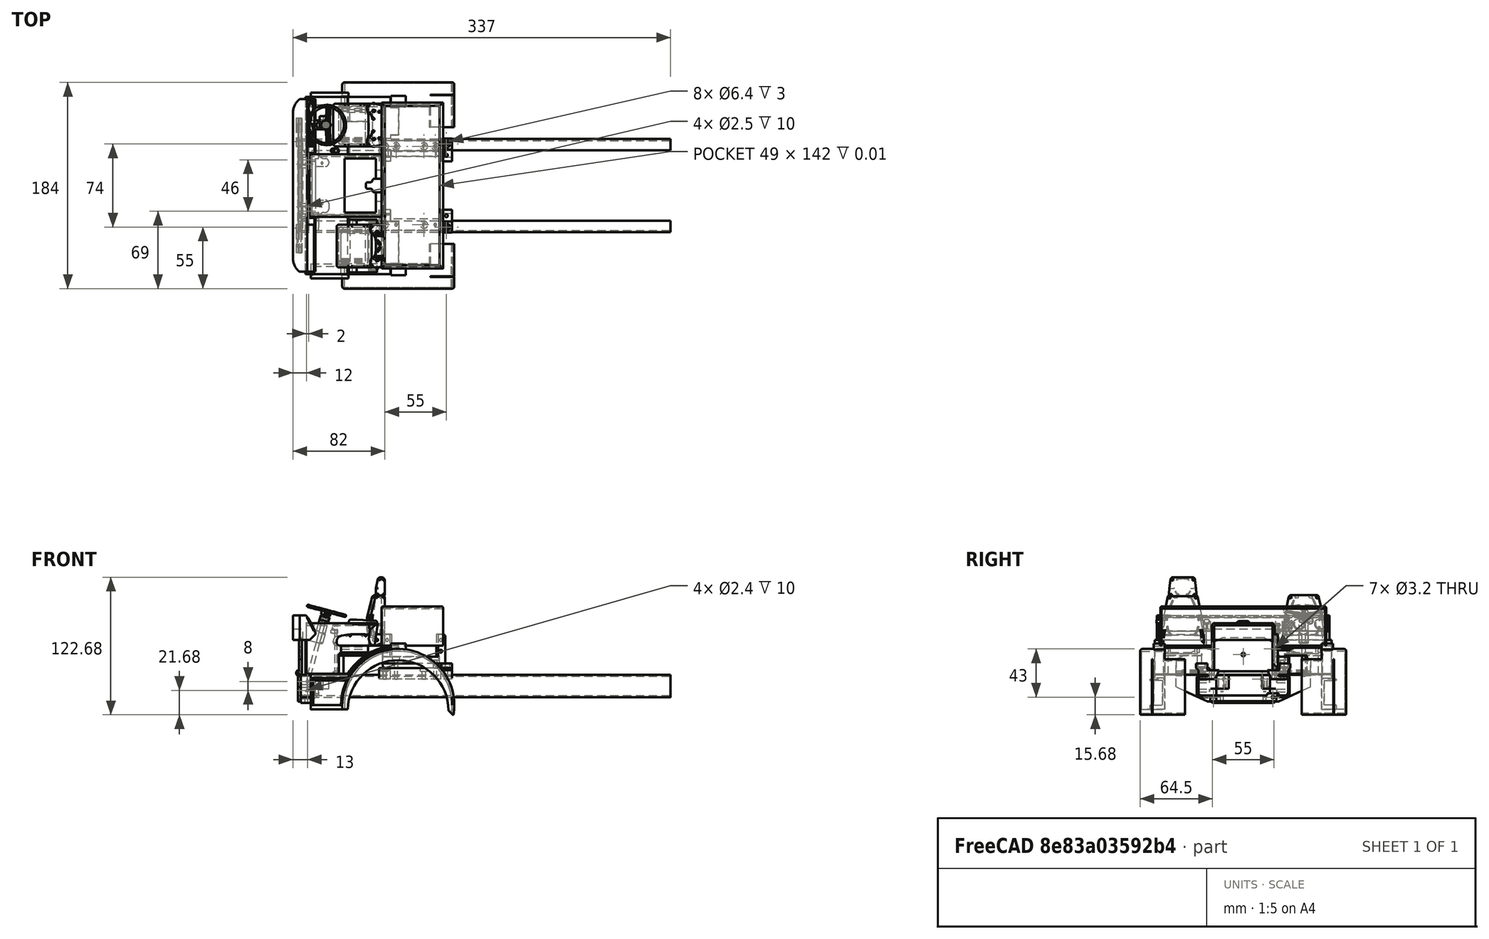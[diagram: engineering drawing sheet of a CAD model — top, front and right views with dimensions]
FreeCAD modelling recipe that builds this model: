
FCSTD DOCUMENT  (FreeCAD 0.16R6188 (Git))
Label: cab-internals
License: All rights reserved
LicenseURL: http://en.wikipedia.org/wiki/All_rights_reserved
objects: Part::Box×137, Part::Cylinder×127, Part::MultiFuse×110, Part::Cut×106, Part::Fillet×98, Part::Chamfer×51, Part::Mirroring×12, Part::Torus×1
note: 642 computed .brp shape members not serialized (recipe doc carries the construction recipe); baked Part::Feature solids carry a one-line shape summary decoded from their .brp

FEATURE [Part::Box] Box001  label="Cube001"
  Height = 64
  Length = 150
  Placement = pos=(0,-1,60) rot=(0,0,1;0rad)
  Width = 170
FEATURE [Part::MultiFuse] Fusion001
FEATURE [Part::Cut] Cut002
FEATURE [Part::Cylinder] Cylinder
  Angle = 360
  Height = 15
  Radius = 2.7
FEATURE [Part::Cylinder] Cylinder001
  Angle = 360
  Height = 15
  Radius = 2.7
FEATURE [Part::Fillet] Fillet008
  Base = -> Cylinder
  Edges = 2 edges r=2: [Edge1,Edge3]
  Placement = pos=(152.5,151,39) rot=(1,0,0;1.5708rad)
FEATURE [Part::Cylinder] Cylinder002
  Angle = 360
  Height = 15
  Radius = 2.7
FEATURE [Part::Fillet] Fillet011
  Base = -> Cylinder001
  Edges = 2 edges r=2: [Edge1,Edge3]
  Placement = pos=(152.5,151,31) rot=(1,0,0;1.5708rad)
FEATURE [Part::Fillet] Fillet012
  Base = -> Cylinder002
  Edges = 2 edges r=2: [Edge1,Edge3]
  Placement = pos=(152.5,31,31) rot=(1,0,0;1.5708rad)
FEATURE [Part::Cylinder] Cylinder004
  Angle = 360
  Height = 15
  Radius = 2.7
FEATURE [Part::Fillet] Fillet010
  Base = -> Cylinder004
  Edges = 2 edges r=2: [Edge1,Edge3]
  Placement = pos=(152.5,31,39) rot=(1,0,0;1.5708rad)
FEATURE [Part::MultiFuse] Fusion006
  Shapes = -> [Fillet008,Fillet010,Fillet011,Fillet012]
FEATURE [Part::MultiFuse] Fusion007
  Shapes = -> [Box001,Fusion006,Fusion001]
FEATURE [Part::Cut] Cut017  label="cab-lower"
  Base = -> Cut002
  Tool = -> Fusion007
FEATURE [Part::Cylinder] Cylinder005
  Angle = 198
  Height = 22
  Placement = pos=(98,168,-23) rot=(1,0,0;1.5708rad)
  Radius = 50
FEATURE [Part::Cylinder] Cylinder006
  Angle = 198
  Height = 22
  Placement = pos=(98.7,168,-28) rot=(1,0,0;1.5708rad)
  Radius = 45
FEATURE [Part::Cylinder] Cylinder003
  Angle = 198
  Height = 22
  Placement = pos=(98,167,-23) rot=(1,0,0;1.5708rad)
  Radius = 48
FEATURE [Part::Cut] Cut009
  Base = -> Cylinder005
  Tool = -> Cylinder006
FEATURE [Part::Cut] Cut010
  Base = -> Cut009
  Placement = pos=(5.48275,6,16.6681) rot=(0,1,0;0.174533rad)
  Tool = -> Cylinder003
FEATURE [Part::Cylinder] Cylinder007
  Angle = 360
  Height = 22
  Placement = pos=(98,174,-23) rot=(1,0,0;1.5708rad)
  Radius = 50
FEATURE [Part::Box] Box011  label="Cube011"
  Height = 27
  Length = 34
  Placement = pos=(20,152,-27) rot=(0,0,1;0rad)
  Width = 16
FEATURE [Part::Box] Box012  label="Cube012"
  Height = 27
  Length = 30
  Placement = pos=(32,152,-54) rot=(0,0,1;0rad)
  Width = 22
FEATURE [Part::Cut] Cut012
  Base = -> Box011
  Tool = -> Cylinder007
FEATURE [Part::Box] Box013  label="Cube013"
  Height = 22
  Length = 31
  Placement = pos=(22,162,-23) rot=(0,0,1;0rad)
  Width = 6
FEATURE [Part::Cylinder] Cylinder008
  Angle = 360
  Height = 22
  Placement = pos=(98,174,-23) rot=(1,0,0;1.5708rad)
  Radius = 50
FEATURE [Part::Cut] Cut016
  Base = -> Cut010
  Tool = -> Box012
FEATURE [Part::Box] Box015  label="Cube015"
  Height = 22
  Length = 35
  Placement = pos=(20,162,-23) rot=(0,0,1;0rad)
  Width = 6
FEATURE [Part::Box] Box016  label="Cube016"
  Height = 22
  Length = 31
  Placement = pos=(22,154,-23) rot=(0,0,1;0rad)
  Width = 8
FEATURE [Part::Cylinder] Cylinder009
  Angle = 360
  Height = 22
  Placement = pos=(98,174,-23) rot=(1,0,0;1.5708rad)
  Radius = 51
FEATURE [Part::Cut] Cut018
  Base = -> Box013
  Tool = -> Cylinder008
FEATURE [Part::Cut] Cut019
  Base = -> Box016
  Tool = -> Cylinder009
FEATURE [Part::Cut] Cut020
  Base = -> Cut012
  Tool = -> Cut018
FEATURE [Part::Cut] Cut021
  Base = -> Cut020
  Tool = -> Cut019
FEATURE [Part::Cut] Cut022
  Base = -> Cut021
  Tool = -> Box015
FEATURE [Part::MultiFuse] Fusion003
  Shapes = -> [Cut022,Cut016]
FEATURE [Part::Cut] Cut023
  Base = -> Cut021
  Tool = -> Box015
FEATURE [Part::Cut] Cut024
  Base = -> Cut010
  Tool = -> Box012
FEATURE [Part::MultiFuse] Fusion004  label="right-wing_00"
  Placement = pos=(0,1,0) rot=(0,0,1;0rad)
  Shapes = -> [Cut023,Cut024]
FEATURE [Part::Mirroring] Part__Mirroring  label="left-wing_00"
  Base = (0,0,0)
  Normal = (0,1,0)
  Placement = pos=(0,167,0) rot=(0,0,1;0rad)
  Source = -> Fusion003
FEATURE [Part::Cylinder] Cylinder018
  Angle = 360
  Height = 22
  Placement = pos=(98,189,-23) rot=(1,0,0;1.5708rad)
  Radius = 50
FEATURE [Part::Cylinder] Cylinder019
  Angle = 360
  Height = 22
  Placement = pos=(98,189,-23) rot=(1,0,0;1.5708rad)
  Radius = 82
FEATURE [Part::Cut] Cut088
  Base = -> Cylinder019
  Placement = pos=(0,-1,0) rot=(0,0,1;0rad)
  Tool = -> Cylinder018
FEATURE [Part::Cut] Cut089
  Base = -> Fusion004
  Tool = -> Cut088
FEATURE [Part::Cylinder] Cylinder020
  Angle = 360
  Height = 22
  Placement = pos=(98,189,-23) rot=(1,0,0;1.5708rad)
  Radius = 82
FEATURE [Part::Cylinder] Cylinder021
  Angle = 360
  Height = 22
  Placement = pos=(98,189,-23) rot=(1,0,0;1.5708rad)
  Radius = 50
FEATURE [Part::Cut] Cut090
  Base = -> Cylinder020
  Placement = pos=(0,-187,0) rot=(0,0,1;0rad)
  Tool = -> Cylinder021
FEATURE [Part::Cut] Cut091
  Base = -> Part__Mirroring
  Tool = -> Cut090
FEATURE [Part::Fillet] Fillet098
  Base = -> Cut091
  Edges = 1 edges r=2: [Edge58]
FEATURE [Part::Fillet] Fillet099
  Base = -> Cut089
  Edges = 1 edges r=2: [Edge58]
FEATURE [Part::Fillet] Fillet101
  Base = -> Fillet098
  Edges = 1 edges r=2: [Edge37]
FEATURE [Part::Box] Box188  label="Cube188"
  Height = 5.8
  Length = 13.6
  Placement = pos=(91.2,5,26) rot=(0,0,1;0rad)
  Width = 10
FEATURE [Part::Box] Box192  label="Cube192"
  Height = 5.8
  Length = 13.6
  Placement = pos=(91.2,153,26) rot=(0,0,1;0rad)
  Width = 10
FEATURE [Part::MultiFuse] Fusion078  label="left-wing_01"
  Shapes = -> [Fillet101,Box188]
FEATURE [Part::MultiFuse] Fusion079
  Shapes = -> [Box192,Fillet099]
FEATURE [Part::Fillet] Fillet102  label="right-wing_01"
  Base = -> Fusion079
  Edges = 1 edges r=2: [Edge72]
FEATURE [Part::Box] Box204  label="Cube204"
  Height = 10
  Length = 10
  Placement = pos=(140.3,-7,-39.5) rot=(0,-1,0;0.785398rad)
  Width = 40
FEATURE [Part::Cylinder] Cylinder043
  Angle = 65
  Height = 18
  Placement = pos=(98,153,-23) rot=(0.992433,0.086827,-0.086827;1.57839rad)
  Radius = 50
FEATURE [Part::Cylinder] Cylinder044
  Angle = 360
  Height = 18
  Placement = pos=(98,153,-23) rot=(1,0,0;1.5708rad)
  Radius = 48
FEATURE [Part::Cut] Cut107
  Base = -> Cylinder043
  Tool = -> Cylinder044
FEATURE [Part::Cylinder] Cylinder045
  Angle = 360
  Height = 18
  Placement = pos=(98,153,-23) rot=(1,0,0;1.5708rad)
  Radius = 48
FEATURE [Part::Cylinder] Cylinder046
  Angle = 65
  Height = 18
  Placement = pos=(98,153,-23) rot=(0.992433,0.086827,-0.086827;1.57839rad)
  Radius = 50
FEATURE [Part::Cut] Cut108
  Base = -> Cylinder046
  Placement = pos=(0,-120,0) rot=(0,0,1;0rad)
  Tool = -> Cylinder045
FEATURE [Part::MultiFuse] Fusion100
  Shapes = -> [Fusion078,Cut108]
FEATURE [Part::Cut] Cut109
  Base = -> Fusion100
  Placement = pos=(0,-2,0) rot=(0,0,1;0rad)
  Tool = -> Box204
FEATURE [Part::MultiFuse] Fusion101
  Shapes = -> [Cut107,Fillet102]
FEATURE [Part::Box] Box205  label="Cube205"
  Height = 10
  Length = 10
  Placement = pos=(140.3,135,-39.5) rot=(0,-1,0;0.785398rad)
  Width = 40
FEATURE [Part::Cut] Cut110
  Base = -> Fusion101
  Placement = pos=(0,2,0) rot=(0,0,1;0rad)
  Tool = -> Box205
FEATURE [Part::Cylinder] Cylinder047
  Angle = 65
  Height = 0.5
  Placement = pos=(98,153,-23) rot=(0.992433,0.086827,-0.086827;1.57839rad)
  Radius = 50
FEATURE [Part::Cylinder] Cylinder048
  Angle = 360
  Height = 0.5
  Placement = pos=(98,153,-23) rot=(1,0,0;1.5708rad)
  Radius = 49.5
FEATURE [Part::Cut] Cut111
  Base = -> Cylinder047
  Placement = pos=(0,-151,0) rot=(0,0,1;0rad)
  Tool = -> Cylinder048
FEATURE [Part::Cylinder] Cylinder049
  Angle = 65
  Height = 0.5
  Placement = pos=(98,153,-23) rot=(0.992433,0.086827,-0.086827;1.57839rad)
  Radius = 50
FEATURE [Part::Cylinder] Cylinder050
  Angle = 360
  Height = 0.5
  Placement = pos=(98,153,-23) rot=(1,0,0;1.5708rad)
  Radius = 49.5
FEATURE [Part::Cut] Cut112
  Base = -> Cylinder049
  Placement = pos=(0,13,0) rot=(0,0,1;0rad)
  Tool = -> Cylinder050
FEATURE [Part::Cut] Cut113  label="left-wing"
  Base = -> Cut109
  Placement = pos=(0,1,0) rot=(0,0,1;0rad)
  Tool = -> Cut111
FEATURE [Part::Cut] Cut114  label="right-wing"
  Base = -> Cut110
  Placement = pos=(0,-1,0) rot=(0,0,1;0rad)
  Tool = -> Cut112
FEATURE [Part::Box] Box007  label="Cube"
  Height = 20
  Length = 330
  Width = 10
FEATURE [Part::Box] Box008  label="Cube206"
  Height = 17
  Length = 430
  Placement = pos=(0,1.5,1.5) rot=(0,0,1;0rad)
  Width = 10
FEATURE [Part::Fillet] Fillet
  Base = -> Box007
  Edges = 2 edges r=3: [Edge9,Edge10]
FEATURE [Part::Fillet] Fillet001
  Base = -> Box008
  Edges = 2 edges r=2: [Edge9,Edge10]
FEATURE [Part::Cut] Cut003
  Base = -> Fillet
  Tool = -> Fillet001
FEATURE [Part::Fillet] Fillet002
  Base = -> Box007
  Edges = 2 edges r=3: [Edge9,Edge10]
FEATURE [Part::Fillet] Fillet003
  Base = -> Box008
  Edges = 2 edges r=2: [Edge9,Edge10]
FEATURE [Part::Cut] Cut004
  Base = -> Fillet002
  Placement = pos=(0,-1.5,0) rot=(0,0,1;0rad)
  Tool = -> Fillet003
FEATURE [Part::Mirroring] Part__Mirroring001  label="Cut (Mirror #1)"
  Base = (0,0,0)
  Normal = (0,1,0)
  Placement = pos=(0,81.5,0) rot=(0,0,1;0rad)
  Source = -> Cut003
FEATURE [Part::Fillet] Fillet004  label="lower-plate_00"
  Edges = 2 edges r=0.25: [Edge74,Edge75]
  Placement = pos=(-3,100,59) rot=(-0.57735,0.57735,0.57735;4.18879rad)
FEATURE [Part::Cylinder] Cylinder051
  Angle = 360
  Height = 11
  Placement = pos=(-2,66.5,-1) rot=(0,1,0;1.5708rad)
  Radius = 1.25
FEATURE [Part::Cylinder] Cylinder010
  Angle = 360
  Height = 11
  Placement = pos=(-2,13.5,-1) rot=(0,1,0;1.5708rad)
  Radius = 1.25
FEATURE [Part::Cylinder] Cylinder011
  Angle = 360
  Height = 15
  Placement = pos=(-2,23,15) rot=(0,1,0;1.5708rad)
  Radius = 1.25
FEATURE [Part::Cylinder] Cylinder012
  Angle = 360
  Height = 15
  Placement = pos=(-2,57,15) rot=(0,1,0;1.5708rad)
  Radius = 1.25
FEATURE [Part::MultiFuse] Fusion010
  Placement = pos=(0,0,1) rot=(0,0,1;0rad)
  Shapes = -> [Cylinder051,Cylinder011,Cylinder010,Cylinder012]
FEATURE [Part::Cut] Cut005
  Tool = -> Fusion010
FEATURE [Part::Cylinder] Cylinder013
  Angle = 360
  Height = 2.5
  Placement = pos=(-4.5,12.5,-1) rot=(0,1,0;1.5708rad)
  Radius = 2
FEATURE [Part::Cylinder] Cylinder014
  Angle = 360
  Height = 2.5
  Placement = pos=(-4.5,67.5,-1) rot=(0,1,0;1.5708rad)
  Radius = 2
FEATURE [Part::Cylinder] Cylinder015
  Angle = 360
  Height = 11
  Placement = pos=(-7,66.5,-1) rot=(0,1,0;1.5708rad)
  Radius = 1.6
FEATURE [Part::Cylinder] Cylinder016
  Angle = 360
  Height = 11
  Placement = pos=(-7,13.5,-1) rot=(0,1,0;1.5708rad)
  Radius = 1.6
FEATURE [Part::MultiFuse] Fusion011
  Shapes = -> [Cylinder016,Cylinder015]
FEATURE [Part::MultiFuse] Fusion012
  Shapes = -> [Cylinder014,Cylinder013]
FEATURE [Part::MultiFuse] Fusion013
  Shapes = -> [Fillet004,Fusion012]
FEATURE [Part::Cut] Cut006  label="cab_tilt_lower001"
  Base = -> Fusion013
  Placement = pos=(13,44,-15) rot=(0,0,1;0rad)
  Tool = -> Fusion011
FEATURE [Part::Fillet] Fillet009
  Base = -> Cut005
  Edges = 2 edges r=3: [Edge4,Edge16]
FEATURE [Part::MultiFuse] Fusion015  label="frame-bars001"
  Placement = pos=(11,44,-16) rot=(0,0,1;0rad)
  Shapes = -> [Cut004,Part__Mirroring001]
FEATURE [Part::Cut] Cut007  label="cab_tilt_upper001"
  Placement = pos=(11,144,37) rot=(0.57735,-0.57735,-0.57735;2.0944rad)
FEATURE [Part::Cylinder] Cylinder033
  Angle = 360
  Height = 10
  Placement = pos=(-8,25.5,0) rot=(0,0,1;0rad)
  Radius = 1.2
FEATURE [Part::Cylinder] Cylinder034
  Angle = 360
  Height = 10
  Placement = pos=(-8,33.5,0) rot=(0,0,1;0rad)
  Radius = 1.2
FEATURE [Part::MultiFuse] Fusion022
  Placement = pos=(12,80,-19.5) rot=(1,0,0;1.5708rad)
  Shapes = -> [Cylinder034,Cylinder033]
FEATURE [Part::Cylinder] Cylinder035
  Angle = 360
  Height = 10
  Placement = pos=(-8,33.5,0) rot=(0,0,1;0rad)
  Radius = 1.2
FEATURE [Part::Cylinder] Cylinder036
  Angle = 360
  Height = 10
  Placement = pos=(-8,25.5,0) rot=(0,0,1;0rad)
  Radius = 1.2
FEATURE [Part::MultiFuse] Fusion023
  Placement = pos=(12,10,-19.5) rot=(1,0,0;1.5708rad)
  Shapes = -> [Cylinder035,Cylinder036]
FEATURE [Part::MultiFuse] Fusion024
  Shapes = -> [Fusion022,Fusion023]
FEATURE [Part::Cut] Cut115  label="front-cross-member__"
  Base = -> Fillet009
  Tool = -> Fusion024
FEATURE [Part::Box] Box031
  Height = 1
  Length = 16
  Placement = pos=(-2,9,18.5) rot=(0,0,1;0rad)
  Width = 62
FEATURE [Part::MultiFuse] Fusion041  label="front-cross-member_"
  Shapes = -> [Cut115,Box031]
FEATURE [Part::Box] Box035  label="Cube024"
  Height = 25
  Length = 7
  Placement = pos=(8,16,-5) rot=(0,0,1;0rad)
  Width = 48
FEATURE [Part::Cut] Cut046
  Base = -> Fusion041
  Tool = -> Box035
FEATURE [Part::Box] Box036  label="Cube025"
  Height = 12
  Length = 15
  Placement = pos=(8,16,7.5) rot=(0,0,1;0rad)
  Width = 7
FEATURE [Part::Box] Box038  label="Cube027"
  Height = 18
  Length = 3
  Placement = pos=(8,16,1.5) rot=(0,0,1;0rad)
  Width = 48
FEATURE [Part::Box] Box039  label="Cube028"
  Height = 12
  Length = 12
  Placement = pos=(11,53,7.5) rot=(0,0,1;0rad)
  Width = 11
FEATURE [Part::Cylinder] Cylinder059
  Angle = 360
  Height = 15
  Placement = pos=(17,19.5,1.5) rot=(0,0,1;0rad)
  Radius = 0.9
FEATURE [Part::Cylinder] Cylinder060
  Angle = 360
  Height = 15
  Placement = pos=(17,55.5,1.5) rot=(0,0,1;0rad)
  Radius = 0.9
FEATURE [Part::MultiFuse] Fusion044
  Placement = pos=(0,0.5,4) rot=(0,0,1;0rad)
  Shapes = -> [Cylinder059,Cylinder060]
FEATURE [Part::Cylinder] Cylinder061
  Angle = 360
  Height = 10
  Placement = pos=(-2,23,16) rot=(0,1,0;1.5708rad)
  Radius = 1.25
FEATURE [Part::Cylinder] Cylinder062
  Angle = 360
  Height = 10
  Placement = pos=(-2,57,16) rot=(0,1,0;1.5708rad)
  Radius = 1.25
FEATURE [Part::MultiFuse] Fusion045
  Shapes = -> [Cylinder062,Cylinder061]
FEATURE [Part::Cylinder] Cylinder063
  Angle = 360
  Height = 10
  Placement = pos=(-2,23,16) rot=(0,1,0;1.5708rad)
  Radius = 1.25
FEATURE [Part::Cylinder] Cylinder064
  Angle = 360
  Height = 10
  Placement = pos=(-2,57,16) rot=(0,1,0;1.5708rad)
  Radius = 1.25
FEATURE [Part::MultiFuse] Fusion046
  Placement = pos=(0,0,-6) rot=(0,0,1;0rad)
  Shapes = -> [Cylinder064,Cylinder063]
FEATURE [Part::MultiFuse] Fusion047
  Shapes = -> [Cut046,Box036,Box038,Box039]
FEATURE [Part::Cut] Cut047
  Base = -> Fusion047
  Tool = -> Fusion044
FEATURE [Part::MultiFuse] Fusion048
  Shapes = -> [Fusion045,Cut047]
FEATURE [Part::Cut] Cut048
  Base = -> Fusion048
  Tool = -> Fusion046
FEATURE [Part::Mirroring] Part__Mirroring006  label="Cut048 (Mirror #5)"
  Base = (0,0,0)
  Normal = (0,1,0)
  Source = -> Cut048
FEATURE [Part::Fillet] Fillet034
  Base = -> Part__Mirroring006
  Edges = 2 edges r=5: [Edge102,Edge118]
FEATURE [Part::Fillet] Fillet035
  Base = -> Fillet034
  Edges = 4 edges r=3: [Edge33,Edge54,Edge77,Edge79]
FEATURE [Part::Box] Box040
  Height = 10
  Length = 10
  Placement = pos=(8,-18.5,-6.5) rot=(0,0,1;0rad)
  Width = 10
FEATURE [Part::Cut] Cut049
  Base = -> Fillet035
  Tool = -> Box040
FEATURE [Part::Cylinder] Cylinder065
  Angle = 360
  Height = 10
  Placement = pos=(3,-59,-5) rot=(0,0,1;0rad)
  Radius = 1.25
FEATURE [Part::Cylinder] Cylinder066
  Angle = 360
  Height = 10
  Placement = pos=(3,-21,-5) rot=(0,0,1;0rad)
  Radius = 1.25
FEATURE [Part::MultiFuse] Fusion049
  Shapes = -> [Cylinder065,Cylinder066]
FEATURE [Part::Cylinder] Cylinder067
  Angle = 360
  Height = 10
  Placement = pos=(5,-63,9.5) rot=(0,0,1;0rad)
  Radius = 1.25
FEATURE [Part::Cylinder] Cylinder068
  Angle = 360
  Height = 10
  Placement = pos=(5,-17,9.5) rot=(0,0,1;0rad)
  Radius = 1.25
FEATURE [Part::MultiFuse] Fusion050
  Shapes = -> [Cylinder067,Cylinder068]
FEATURE [Part::Cut] Cut050
  Base = -> Cut049
  Tool = -> Fusion049
FEATURE [Part::Cut] Cut051  label="front-cross-member"
  Base = -> Cut050
  Placement = pos=(13,124,-16) rot=(0,0,1;0rad)
  Tool = -> Fusion050
FEATURE [Part::Box] Box  label="Cube207"
  Height = 10
  Length = 65
  Width = 80
FEATURE [Part::Box] Box206  label="Cube208"
  Height = 10
  Length = 65
  Placement = pos=(0,19,0) rot=(0,0,1;0rad)
  Width = 42
FEATURE [Part::Cylinder] Cylinder069
  Angle = 360
  Height = 10
  Radius = 1.25
FEATURE [Part::Cylinder] Cylinder070
  Angle = 360
  Height = 10
  Placement = pos=(0,54,0) rot=(0,0,1;0rad)
  Radius = 1.25
FEATURE [Part::MultiFuse] Fusion
  Placement = pos=(5,13,0) rot=(0,0,1;0rad)
  Shapes = -> [Cylinder069,Cylinder070]
FEATURE [Part::Cylinder] Cylinder071
  Angle = 360
  Height = 10
  Placement = pos=(0,54,0) rot=(0,0,1;0rad)
  Radius = 1.25
FEATURE [Part::Cylinder] Cylinder072
  Angle = 360
  Height = 10
  Radius = 1.25
FEATURE [Part::MultiFuse] Fusion102
  Placement = pos=(60,13,0) rot=(0,0,1;0rad)
  Shapes = -> [Cylinder072,Cylinder071]
FEATURE [Part::MultiFuse] Fusion002
  Shapes = -> [Fusion,Fusion102]
FEATURE [Part::Cylinder] Cylinder073
  Angle = 360
  Height = 10
  Placement = pos=(5,0,0) rot=(0,0,1;0rad)
  Radius = 1.6
FEATURE [Part::Cylinder] Cylinder074
  Angle = 360
  Height = 10
  Placement = pos=(5,70,0) rot=(0,0,1;0rad)
  Radius = 1.6
FEATURE [Part::MultiFuse] Fusion103
  Placement = pos=(0,5,0) rot=(0,0,1;0rad)
  Shapes = -> [Cylinder074,Cylinder073]
FEATURE [Part::Cylinder] Cylinder075
  Angle = 360
  Height = 3
  Placement = pos=(5,70,0) rot=(0,0,1;0rad)
  Radius = 3.2
FEATURE [Part::Cylinder] Cylinder076
  Angle = 360
  Height = 3
  Placement = pos=(5,0,0) rot=(0,0,1;0rad)
  Radius = 3.2
FEATURE [Part::MultiFuse] Fusion104
  Placement = pos=(0,5,7) rot=(0,0,1;0rad)
  Shapes = -> [Cylinder075,Cylinder076]
FEATURE [Part::MultiFuse] Fusion005
  Placement = pos=(55,0,0) rot=(0,0,1;0rad)
  Shapes = -> [Fusion103,Fusion104]
FEATURE [Part::MultiFuse] Fusion105
  Placement = pos=(0,5,7) rot=(0,0,1;0rad)
  Shapes = -> [Cylinder075,Cylinder076]
FEATURE [Part::MultiFuse] Fusion008
  Placement = pos=(0,5,0) rot=(0,0,1;0rad)
  Shapes = -> [Cylinder074,Cylinder073]
FEATURE [Part::MultiFuse] Fusion106
  Placement = pos=(20,0,0) rot=(0,0,1;0rad)
  Shapes = -> [Fusion008,Fusion105]
FEATURE [Part::MultiFuse] Fusion009
  Shapes = -> [Fusion005,Fusion106]
FEATURE [Part::Cylinder] Cylinder077
  Angle = 360
  Height = 10
  Placement = pos=(0,70,0) rot=(0,0,1;0rad)
  Radius = 1.25
FEATURE [Part::Cylinder] Cylinder078
  Angle = 360
  Height = 10
  Radius = 1.25
FEATURE [Part::Box] Box002  label="Cube002"
  Height = 10
  Length = 10
  Placement = pos=(0,-2,4) rot=(0,0,1;0rad)
  Width = 10
FEATURE [Part::Chamfer] Chamfer002
  Base = -> Box002
  Edges = 1 edges r=6: [Edge9]
FEATURE [Part::Cut] Cut
  Base = -> Box
  Tool = -> Box206
FEATURE [Part::Box] Box003
  Height = 10
  Length = 45
  Placement = pos=(10,10,0) rot=(0,0,1;0rad)
  Width = 9
FEATURE [Part::Box] Box004
  Height = 10
  Length = 45
  Placement = pos=(10,61,0) rot=(0,0,1;0rad)
  Width = 9
FEATURE [Part::MultiFuse] Fusion107
  Shapes = -> [Box003,Box004]
FEATURE [Part::Cut] Cut116
  Base = -> Cut
  Tool = -> Fusion107
FEATURE [Part::Cut] Cut117
  Base = -> Cut116
  Tool = -> Fusion002
FEATURE [Part::MultiFuse] Fusion108
  Placement = pos=(50,5,0) rot=(0,0,1;0rad)
  Shapes = -> [Cylinder077,Cylinder078]
FEATURE [Part::Cylinder] Cylinder079
  Angle = 360
  Height = 10
  Radius = 1.25
FEATURE [Part::Cylinder] Cylinder080
  Angle = 360
  Height = 10
  Placement = pos=(0,70,0) rot=(0,0,1;0rad)
  Radius = 1.25
FEATURE [Part::MultiFuse] Fusion109
  Placement = pos=(15,5,0) rot=(0,0,1;0rad)
  Shapes = -> [Cylinder080,Cylinder079]
FEATURE [Part::Box] Box005
  Height = 12
  Length = 65
  Placement = pos=(0,15,0) rot=(-1,0,0;0.401426rad)
  Width = 10
FEATURE [Part::Mirroring] Part__Mirroring007  label="Box005 (Mirror #1)"
  Base = (0,0,0)
  Normal = (0,1,0)
  Placement = pos=(0,80,0) rot=(0,0,1;0rad)
  Source = -> Box005
FEATURE [Part::Box] Box006
  Height = 12
  Length = 65
  Placement = pos=(0,15,0) rot=(-1,0,0;0.401426rad)
  Width = 10
FEATURE [Part::MultiFuse] Fusion110
  Shapes = -> [Part__Mirroring007,Box006]
FEATURE [Part::Cut] Cut008
  Base = -> Cut117
  Tool = -> Fusion110
FEATURE [Part::MultiFuse] Fusion014
  Shapes = -> [Fusion009,Fusion108,Fusion109]
FEATURE [Part::Cut] Cut118
  Base = -> Cut008
  Tool = -> Fusion014
FEATURE [Part::Box] Box207  label="Cube003"
  Height = 10
  Length = 10
  Placement = pos=(0,-2,4) rot=(0,0,1;0rad)
  Width = 10
FEATURE [Part::Chamfer] Chamfer
  Base = -> Box207
  Edges = 1 edges r=6: [Edge9]
FEATURE [Part::Mirroring] Part__Mirroring008  label="Chamfer (Mirror #2)"
  Base = (0,0,0)
  Normal = (0,1,0)
  Placement = pos=(0,80,0) rot=(0,0,1;0rad)
  Source = -> Chamfer
FEATURE [Part::MultiFuse] Fusion111
  Shapes = -> [Chamfer002,Cut118,Part__Mirroring008]
FEATURE [Part::Cylinder] Cylinder081
  Angle = 360
  Height = 10
  Placement = pos=(5,3,4) rot=(0,0,1;0rad)
  Radius = 1.25
FEATURE [Part::Cylinder] Cylinder017
  Angle = 360
  Height = 3
  Placement = pos=(5,3,11) rot=(0,0,1;0rad)
  Radius = 3.2
FEATURE [Part::MultiFuse] Fusion016
  Shapes = -> [Cylinder081,Cylinder017]
FEATURE [Part::Cylinder] Cylinder082
  Angle = 360
  Height = 3
  Placement = pos=(5,3,11) rot=(0,0,1;0rad)
  Radius = 3.2
FEATURE [Part::Cylinder] Cylinder083
  Angle = 360
  Height = 10
  Placement = pos=(5,3,4) rot=(0,0,1;0rad)
  Radius = 1.25
FEATURE [Part::MultiFuse] Fusion017
  Placement = pos=(0,74,0) rot=(0,0,1;0rad)
  Shapes = -> [Cylinder083,Cylinder082]
FEATURE [Part::MultiFuse] Fusion018
  Shapes = -> [Fusion016,Fusion017]
FEATURE [Part::Cut] Cut119
  Base = -> Fusion111
  Tool = -> Fusion018
FEATURE [Part::Box] Box208
  Height = 2
  Length = 10
  Placement = pos=(0,8,8) rot=(0,0,1;0rad)
  Width = 11
FEATURE [Part::Box] Box009
  Height = 2
  Length = 10
  Placement = pos=(0,61,8) rot=(0,0,1;0rad)
  Width = 11
FEATURE [Part::Box] Box010
  Height = 2
  Length = 10
  Placement = pos=(55,8,8) rot=(0,0,1;0rad)
  Width = 11
FEATURE [Part::Box] Box209
  Height = 2
  Length = 10
  Placement = pos=(55,61,8) rot=(0,0,1;0rad)
  Width = 11
FEATURE [Part::MultiFuse] Fusion019
  Shapes = -> [Box208,Box010,Box209,Box009]
FEATURE [Part::Cut] Cut011  label="gearbox-holder"
  Base = -> Cut119
  Placement = pos=(146,124,0) rot=(0,0,1;3.14159rad)
  Tool = -> Fusion019
FEATURE [Part::Box] Box210
  Height = 5
  Length = 56
  Placement = pos=(-14,1,0) rot=(0,0,1;0rad)
  Width = 10
FEATURE [Part::Cut] Cut120
  Placement = pos=(-18,19,0) rot=(0,0,1;0rad)
FEATURE [Part::Fillet] Fillet103
  Base = -> Cut120
  Edges = 1 edges r=0.6: [Edge14]
  Placement = pos=(29,0,0) rot=(0,0,1;0rad)
FEATURE [Part::Box] Box211
  Height = 10
  Length = 17
  Placement = pos=(20,22,0) rot=(0,0,1;0rad)
  Width = 10
FEATURE [Part::Box] Box014
  Height = 10
  Length = 9
  Placement = pos=(20,11,0) rot=(0,0,1;0rad)
  Width = 21
FEATURE [Part::MultiFuse] Fusion020
  Shapes = -> [Box211,Box014]
FEATURE [Part::Cut] Cut013
  Base = -> Fillet103
  Tool = -> Fusion020
FEATURE [Part::Box] Box212
  Height = 3.4
  Length = 21
  Placement = pos=(8,11,0) rot=(0,0,1;0rad)
  Width = 5
FEATURE [Part::MultiFuse] Fusion021
  Shapes = -> [Box210,Cut013,Box212]
FEATURE [Part::Box] Box213
  Height = 5
  Length = 8
  Placement = pos=(34,-19,0) rot=(0,0,1;0rad)
  Width = 20
FEATURE [Part::Box] Box017
  Height = 5
  Length = 8
  Placement = pos=(-14,-19,0) rot=(0,0,1;0rad)
  Width = 20
FEATURE [Part::Cylinder] Cylinder084
  Angle = 360
  Height = 10
  Placement = pos=(-10,0,0) rot=(0,0,1;0rad)
  Radius = 1.25
FEATURE [Part::Cylinder] Cylinder085
  Angle = 360
  Height = 10
  Placement = pos=(-10,-10,0) rot=(0,0,1;0rad)
  Radius = 1.25
FEATURE [Part::MultiFuse] Fusion112
  Placement = pos=(0,-4,0) rot=(0,0,1;0rad)
  Shapes = -> [Cylinder085,Cylinder084]
FEATURE [Part::Cylinder] Cylinder022
  Angle = 360
  Height = 10
  Placement = pos=(-10,0,0) rot=(0,0,1;0rad)
  Radius = 1.25
FEATURE [Part::Cylinder] Cylinder023
  Angle = 360
  Height = 10
  Placement = pos=(-10,-10,0) rot=(0,0,1;0rad)
  Radius = 1.25
FEATURE [Part::MultiFuse] Fusion113
  Placement = pos=(48,-4,0) rot=(0,0,1;0rad)
  Shapes = -> [Cylinder023,Cylinder022]
FEATURE [Part::Box] Box018
  Height = 3.4
  Length = 17
  Placement = pos=(-9,11,0) rot=(0,0,1;0rad)
  Width = 15
FEATURE [Part::MultiFuse] Fusion114
  Shapes = -> [Fusion112,Fusion113]
FEATURE [Part::Cylinder] Cylinder024
  Angle = 360
  Height = 10
  Placement = pos=(5,19,0) rot=(0,0,1;0rad)
  Radius = 1.6
FEATURE [Part::Cylinder] Cylinder025
  Angle = 360
  Height = 10
  Placement = pos=(-6,19,0) rot=(0,0,1;0rad)
  Radius = 1.6
FEATURE [Part::MultiFuse] Fusion025
  Shapes = -> [Cylinder024,Cylinder025]
FEATURE [Part::Cut] Cut014
  Base = -> Box018
  Tool = -> Fusion025
FEATURE [Part::MultiFuse] Fusion026
  Shapes = -> [Box213,Box017,Cut014,Fusion021]
FEATURE [Part::Cut] Cut015
  Base = -> Fusion026
  Tool = -> Fusion114
FEATURE [Part::Fillet] Fillet104
  Base = -> Cut015
  Edges = 6 edges r=2: [Edge51,Edge54,Edge56,Edge58,Edge59,Edge61]
FEATURE [Part::Fillet] Fillet105
  Base = -> Fillet104
  Edges = 1 edges r=1.5: [Edge36]
FEATURE [Part::Fillet] Fillet106
  Base = -> Fillet105
  Edges = 2 edges r=3: [Edge30,Edge33]
FEATURE [Part::Box] Box019
  Height = 1.6
  Length = 19
  Placement = pos=(-10,10,3.4) rot=(0,0,1;0rad)
  Width = 10
FEATURE [Part::Cut] Cut121
  Base = -> Fillet106
  Tool = -> Box019
FEATURE [Part::Fillet] Fillet107
  Base = -> Cut121
  Edges = 2 edges r=2: [Edge42,Edge63]
FEATURE [Part::Box] Box020
  Height = 1
  Length = 4
  Placement = pos=(-2.5,25,0) rot=(0,0,1;0rad)
  Width = 1
FEATURE [Part::Cut] Cut122
  Base = -> Fillet107
  Tool = -> Box020
FEATURE [Part::Fillet] Fillet005
  Base = -> Cut122
  Edges = 1 edges r=0.99: [Edge94]
FEATURE [Part::Chamfer] Chamfer003
  Base = -> Fillet005
  Edges = 2 edges r=1.5: [Edge34,Edge36]
FEATURE [Part::MultiFuse] Fusion027
  Placement = pos=(48,-4,0) rot=(0,0,1;0rad)
  Shapes = -> [Cylinder023,Cylinder022]
FEATURE [Part::MultiFuse] Fusion029
  Placement = pos=(0,-4,0) rot=(0,0,1;0rad)
  Shapes = -> [Cylinder085,Cylinder084]
FEATURE [Part::MultiFuse] Fusion028
  Shapes = -> [Fusion029,Fusion027]
FEATURE [Part::Box] Box021
  Height = 5
  Length = 8
  Placement = pos=(34,-19,2) rot=(0,0,1;0rad)
  Width = 25
FEATURE [Part::Box] Box022
  Height = 5
  Length = 8
  Placement = pos=(-14,-19,2) rot=(0,0,1;0rad)
  Width = 25
FEATURE [Part::MultiFuse] Fusion030
  Shapes = -> [Box021,Box022]
FEATURE [Part::Cut] Cut123
  Base = -> Fusion030
  Tool = -> Fusion028
FEATURE [Part::Fillet] Fillet006
  Base = -> Cut123
  Edges = 2 edges r=2: [Edge6,Edge23]
FEATURE [Part::Chamfer] Chamfer004
  Base = -> Fillet006
  Edges = 2 edges r=2: [Edge18,Edge31]
FEATURE [Part::MultiFuse] Fusion031
  Placement = pos=(0,0,21) rot=(-1,0,0;1.5708rad)
  Shapes = -> [Chamfer003,Chamfer004]
FEATURE [Part::Box] Box023
  Height = 15
  Length = 53
  Placement = pos=(-13,0,-5) rot=(0,0,1;0rad)
  Width = 10
FEATURE [Part::Cut] Cut124
  Base = -> Fusion031
  Placement = pos=(0,0,0) rot=(0,0,1;3.14159rad)
  Tool = -> Box023
FEATURE [Part::Box] Box024
  Height = 1
  Length = 19
  Placement = pos=(-9,-5,10) rot=(0,0,1;0rad)
  Width = 5
FEATURE [Part::MultiFuse] Fusion032
  Placement = pos=(53,0,0) rot=(0,0,1;0rad)
  Shapes = -> [Cut124,Box024]
FEATURE [Part::Cylinder] Cylinder026
  Angle = 360
  Height = 10
  Placement = pos=(15,5,10) rot=(0,0,1;0rad)
  Radius = 1.6
FEATURE [Part::Cylinder] Cylinder027
  Angle = 360
  Height = 10
  Placement = pos=(50,5,10) rot=(0,0,1;0rad)
  Radius = 1.6
FEATURE [Part::Box] Box025
  Height = 10
  Length = 43
  Placement = pos=(11,0,10) rot=(0,0,1;0rad)
  Width = 10
FEATURE [Part::Fillet] Fillet007
  Base = -> Box025
  Edges = 1 edges r=3: [Edge4]
  Placement = pos=(0,-1,0) rot=(0,0,1;0rad)
FEATURE [Part::Cylinder] Cylinder028
  Angle = 360
  Height = 3
  Placement = pos=(15,5,17) rot=(0,0,1;0rad)
  Radius = 3.2
FEATURE [Part::Cylinder] Cylinder029
  Angle = 360
  Height = 3
  Placement = pos=(50,5,17) rot=(0,0,1;0rad)
  Radius = 3.2
FEATURE [Part::MultiFuse] Fusion034
  Shapes = -> [Cylinder026,Cylinder027,Cylinder028,Cylinder029]
FEATURE [Part::Box] Box026
  Height = 33
  Length = 56
  Placement = pos=(11,-15,10) rot=(0,0,1;0rad)
  Width = 10
FEATURE [Part::Box] Box027
  Height = 10
  Length = 13
  Placement = pos=(54,0,10) rot=(0,0,1;0rad)
  Width = 10
FEATURE [Part::Fillet] Fillet108
  Base = -> Box027
  Edges = 1 edges r=3: [Edge8]
  Placement = pos=(-5,-1,0) rot=(0,0,1;0rad)
FEATURE [Part::Cut] Cut125
  Base = -> Fusion032
  Placement = pos=(-5,14,0) rot=(0,0,1;0rad)
  Tool = -> Box026
FEATURE [Part::MultiFuse] Fusion035
  Placement = pos=(0,1,0) rot=(0,0,1;0rad)
  Shapes = -> [Fillet108,Fillet007]
FEATURE [Part::MultiFuse] Fusion036
  Shapes = -> [Cut125,Fusion035]
FEATURE [Part::Cut] Cut126
  Base = -> Fusion036
  Tool = -> Fusion034
FEATURE [Part::Box] Box028  label="Cube004"
  Height = 10
  Length = 56
  Placement = pos=(6,15,2) rot=(1,0,0;0.698132rad)
  Width = 10
FEATURE [Part::Cut] Cut127  label="steering-servo-holder"
  Base = -> Cut126
  Placement = pos=(146,124,0) rot=(0,0,1;3.14159rad)
  Tool = -> Box028
FEATURE [Part::Box] Box214  label="Cube209"
  Height = 22
  Length = 10
  Placement = pos=(4,7,35) rot=(0,0,1;0rad)
  Width = 154
FEATURE [Part::Box] Box215  label="Cube210"
  Height = 22
  Length = 10
  Placement = pos=(14,7,35) rot=(0,0,1;0rad)
  Width = 154
FEATURE [Part::Chamfer] Chamfer005
  Base = -> Box215
  Edges = 1 edges: [Edge6 r1=15 r2=8]
FEATURE [Part::Chamfer] Chamfer006
  Base = -> Chamfer005
  Edges = 1 edges r=5: [Edge3]
FEATURE [Part::MultiFuse] Fusion115
  Shapes = -> [Box214,Chamfer006]
FEATURE [Part::Box] Box216  label="Cube211"
  Height = 22
  Length = 17
  Placement = pos=(4,4,35) rot=(0,0,1;0rad)
  Width = 160
FEATURE [Part::Box] Box217  label="Cube212"
  Height = 22
  Length = 18
  Placement = pos=(3,3,35) rot=(0,0,1;0rad)
  Width = 162
FEATURE [Part::Fillet] Fillet109
  Base = -> Box216
  Edges = 2 edges r=15: [Edge1,Edge3]
FEATURE [Part::Cut] Cut128
  Base = -> Box217
  Tool = -> Fillet109
FEATURE [Part::Fillet] Fillet110
  Base = -> Fusion115
  Edges = 4 edges r=2: [Edge2,Edge3,Edge6,Edge9]
FEATURE [Part::Box] Box218  label="Cube213"
  Height = 31
  Length = 9
  Placement = pos=(4,46,14) rot=(0,0,1;0rad)
  Width = 77
FEATURE [Part::Cut] Cut129
  Base = -> Fillet110
  Tool = -> Cut128
FEATURE [Part::Cut] Cut130
  Base = -> Cut129
  Tool = -> Box218
FEATURE [Part::Box] Box219  label="Cube214"
  Height = 45
  Length = 67
  Placement = pos=(16,56,5) rot=(0,0,1;0rad)
  Width = 56
FEATURE [Part::Cylinder] Cylinder086
  Angle = 360
  Height = 184
  Placement = pos=(98,176,-23) rot=(1,0,0;1.5708rad)
  Radius = 53
FEATURE [Part::Box] Box220  label="Cube215"
  Height = 31
  Length = 1
  Placement = pos=(15,5,4) rot=(0,0,1;0rad)
  Width = 53
FEATURE [Part::Cut] Cut131
  Base = -> Box219
  Tool = -> Cylinder086
FEATURE [Part::Box] Box221  label="Cube216"
  Height = 1
  Length = 40
  Placement = pos=(15,5,4) rot=(0,0,1;0rad)
  Width = 53
FEATURE [Part::Box] Box222  label="Cube217"
  Height = 46
  Length = 67
  Placement = pos=(16,58,2) rot=(0,0,1;0rad)
  Width = 52
FEATURE [Part::Cut] Cut132
  Base = -> Cut131
  Tool = -> Box222
FEATURE [Part::Box] Box223  label="Cube218"
  Height = 1
  Length = 28
  Placement = pos=(50,60,49) rot=(0,0,1;0rad)
  Width = 48
FEATURE [Part::Cylinder] Cylinder087
  Angle = 360
  Height = 184
  Placement = pos=(98,176,-23) rot=(1,0,0;1.5708rad)
  Radius = 51
FEATURE [Part::Cylinder] Cylinder088
  Angle = 59.4
  Height = 53
  Placement = pos=(98,5,-23) rot=(0.192433,0.693891,0.693891;3.52181rad)
  Radius = 53
FEATURE [Part::Box] Box230  label="Cube225"
  Height = 46
  Length = 20
  Placement = pos=(16,55.5,4.5) rot=(0,0,1;0rad)
  Width = 57
FEATURE [Part::Fillet] Fillet111
  Base = -> Cut132
  Edges = 2 edges r=3: [Edge9,Edge11]
FEATURE [Part::Box] Box231  label="Cube226"
  Height = 10
  Length = 38
  Placement = pos=(45,11,30) rot=(0,0,1;0rad)
  Width = 38
FEATURE [Part::Box] Box232  label="Cube227"
  Height = 45
  Length = 13
  Placement = pos=(75,11,30) rot=(0,0,1;0rad)
  Width = 38
FEATURE [Part::Box] Box233  label="Cube228"
  Height = 18
  Length = 8
  Placement = pos=(80,17,75) rot=(0,0,1;0rad)
  Width = 26
FEATURE [Part::Fillet] Fillet116
  Base = -> Box230
  Edges = 2 edges r=3: [Edge10,Edge12]
FEATURE [Part::Box] Box236  label="Cube231"
  Height = 3
  Length = 35
  Placement = pos=(20,5,1) rot=(0,0,1;0rad)
  Width = 9
FEATURE [Part::MultiFuse] Fusion116
  Shapes = -> [Box236,Box220,Box221,Cylinder088]
FEATURE [Part::Box] Box237  label="Cube232"
  Height = 4
  Length = 14
  Placement = pos=(91,4,26) rot=(0,0,1;0rad)
  Width = 10.5
FEATURE [Part::Box] Box238  label="Cube233"
  Height = 1
  Length = 40
  Placement = pos=(15,14,3) rot=(0,0,1;0rad)
  Width = 44
FEATURE [Part::Cut] Cut139
  Base = -> Fusion116
  Tool = -> Box238
FEATURE [Part::Cut] Cut140
  Base = -> Cut139
  Tool = -> Cylinder087
FEATURE [Part::Box] Box239  label="Cube234"
  Height = 31
  Length = 1
  Placement = pos=(15,5,4) rot=(0,0,1;0rad)
  Width = 53
FEATURE [Part::Box] Box240  label="Cube235"
  Height = 1
  Length = 40
  Placement = pos=(15,5,4) rot=(0,0,1;0rad)
  Width = 53
FEATURE [Part::Cylinder] Cylinder089
  Angle = 360
  Height = 184
  Placement = pos=(98,176,-23) rot=(1,0,0;1.5708rad)
  Radius = 51
FEATURE [Part::Cylinder] Cylinder090
  Angle = 59.4
  Height = 53
  Placement = pos=(98,5,-23) rot=(0.192433,0.693891,0.693891;3.52181rad)
  Radius = 53
FEATURE [Part::Box] Box241  label="Cube236"
  Height = 3
  Length = 35
  Placement = pos=(20,5,1) rot=(0,0,1;0rad)
  Width = 9
FEATURE [Part::MultiFuse] Fusion117
  Shapes = -> [Box241,Box239,Box240,Cylinder090]
FEATURE [Part::Box] Box242  label="Cube237"
  Height = 4
  Length = 14
  Placement = pos=(91,4,26) rot=(0,0,1;0rad)
  Width = 10.5
FEATURE [Part::Box] Box243  label="Cube238"
  Height = 1
  Length = 40
  Placement = pos=(15,14,3) rot=(0,0,1;0rad)
  Width = 44
FEATURE [Part::Cut] Cut142
  Base = -> Fusion117
  Tool = -> Box243
FEATURE [Part::Cut] Cut143
  Base = -> Cut142
  Tool = -> Cylinder089
FEATURE [Part::Cut] Cut144
  Base = -> Cut143
  Tool = -> Box242
FEATURE [Part::Mirroring] Part__Mirroring009  label="Cut144 (Mirror #6)"
  Base = (0,0,0)
  Normal = (0,1,0)
  Placement = pos=(0,168,0) rot=(0,0,1;0rad)
  Source = -> Cut144
FEATURE [Part::Chamfer] Chamfer012
  Base = -> Box231
  Edges = 2 edges: [Edge2 r1=2 r2=12,Edge6 r1=2 r2=12]
FEATURE [Part::Fillet] Fillet117
  Base = -> Chamfer012
  Edges = 3 edges r=3: [Edge3,Edge13,Edge17]
FEATURE [Part::Fillet] Fillet118
  Base = -> Fillet117
  Edges = 1 edges r=5: [Edge3]
FEATURE [Part::Fillet] Fillet119
  Base = -> Fillet118
  Edges = 6 edges r=2: [Edge7,Edge9,Edge11,Edge18,Edge20,Edge22]
FEATURE [Part::Fillet] Fillet120
  Base = -> Fillet119
  Edges = 2 edges r=20: [Edge23,Edge49]
FEATURE [Part::Chamfer] Chamfer013
  Base = -> Box232
  Edges = 1 edges: [Edge2 r1=20 r2=5]
FEATURE [Part::Chamfer] Chamfer014
  Base = -> Chamfer013
  Edges = 1 edges: [Edge3 r1=15 r2=3]
FEATURE [Part::Fillet] Fillet121
  Base = -> Chamfer014
  Edges = 4 edges r=3: [Edge10,Edge12,Edge17,Edge18]
FEATURE [Part::Fillet] Fillet122
  Base = -> Fillet121
  Edges = 2 edges r=20: [Edge12,Edge16]
FEATURE [Part::Fillet] Fillet123
  Base = -> Fillet122
  Edges = 10 edges r=2: [Edge1,Edge2,Edge4,Edge6,Edge8,Edge15,Edge17,Edge21,Edge25,Edge29]
FEATURE [Part::Box] Box245  label="Cube240"
  Height = 48
  Length = 7
  Placement = pos=(69,12,30) rot=(0,1,0;0.10472rad)
  Width = 36
FEATURE [Part::Box] Box235  label="Cube230"
  Height = 50
  Length = 16
  Placement = pos=(75,0,30) rot=(-0.683576,-0.016559,0.729691;0.239394rad)
  Width = 8
FEATURE [Part::Box] Box246  label="Cube241"
  Height = 50
  Length = 16
  Placement = pos=(75,0,30) rot=(-0.683576,-0.016559,0.729691;0.239394rad)
  Width = 8
FEATURE [Part::Mirroring] Part__Mirroring010  label="Cube241 (Mirror #7)"
  Base = (0,0,0)
  Normal = (0,1,0)
  Placement = pos=(0,60,0) rot=(0,0,1;0rad)
  Source = -> Box246
FEATURE [Part::MultiFuse] Fusion118
  Shapes = -> [Part__Mirroring010,Box235]
FEATURE [Part::Cut] Cut145
  Base = -> Fillet123
  Tool = -> Fusion118
FEATURE [Part::Fillet] Fillet124
  Base = -> Cut145
  Edges = 4 edges r=1.6: [Edge19,Edge23,Edge40,Edge49]
FEATURE [Part::Chamfer] Chamfer015
  Base = -> Box245
  Edges = 2 edges: [Edge10 r1=40 r2=4,Edge12 r1=40 r2=4]
FEATURE [Part::Chamfer] Chamfer016
  Base = -> Chamfer015
  Edges = 2 edges: [Edge11 r1=4 r2=7,Edge18 r1=4 r2=7]
FEATURE [Part::Fillet] Fillet125
  Base = -> Chamfer016
  Edges = 2 edges r=10: [Edge18,Edge24]
  Placement = pos=(-0.75,0,0) rot=(0,0,1;0rad)
FEATURE [Part::Cut] Cut146
  Base = -> Fillet124
  Tool = -> Fillet125
FEATURE [Part::Fillet] Fillet126
  Base = -> Cut146
  Edges = 2 edges r=2.5: [Edge93,Edge106]
FEATURE [Part::Box] Box247  label="Cube242"
  Height = 20
  Length = 10
  Placement = pos=(80,12,75) rot=(-0.484761,0.038152,0.873814;0.179649rad)
  Width = 5
FEATURE [Part::Box] Box248  label="Cube243"
  Height = 20
  Length = 10
  Placement = pos=(80,12,75) rot=(-0.484761,0.038152,0.873814;0.179649rad)
  Width = 5
FEATURE [Part::Mirroring] Part__Mirroring011  label="Cube243 (Mirror #8)"
  Base = (0,0,0)
  Normal = (0,1,0)
  Placement = pos=(0,60,0) rot=(0,0,1;0rad)
  Source = -> Box248
FEATURE [Part::MultiFuse] Fusion119
  Shapes = -> [Box247,Part__Mirroring011]
FEATURE [Part::Cut] Cut147
  Base = -> Box233
  Tool = -> Fusion119
FEATURE [Part::Box] Box249  label="Cube244"
  Height = 20
  Length = 8
  Placement = pos=(65,18,75) rot=(0,0,1;0rad)
  Width = 24
FEATURE [Part::Chamfer] Chamfer017
  Base = -> Box249
  Edges = 2 edges: [Edge10 r1=15 r2=3,Edge12 r1=15 r2=3]
FEATURE [Part::Chamfer] Chamfer018
  Base = -> Chamfer017
  Edges = 2 edges: [Edge11 r1=2 r2=7,Edge18 r1=2 r2=7]
FEATURE [Part::Fillet] Fillet127
  Base = -> Chamfer018
  Edges = 2 edges r=12: [Edge10,Edge21]
  Placement = pos=(-5.5,0,13) rot=(0,1,0;0.174533rad)
FEATURE [Part::Chamfer] Chamfer019
  Base = -> Cut147
  Edges = 1 edges: [Edge1 r1=10 r2=2]
FEATURE [Part::Fillet] Fillet128
  Base = -> Chamfer019
  Edges = 4 edges r=3: [Edge3,Edge10,Edge11,Edge15]
FEATURE [Part::Fillet] Fillet129
  Base = -> Fillet128
  Edges = 2 edges r=2: [Edge9,Edge15]
FEATURE [Part::Cut] Cut148
  Base = -> Fillet129
  Tool = -> Fillet127
FEATURE [Part::Fillet] Fillet130
  Base = -> Cut148
  Edges = 3 edges r=2: [Edge3,Edge44,Edge62]
  Placement = pos=(0,0,-2) rot=(0,0,1;0rad)
FEATURE [Part::Box] Box250  label="Cube245"
  Height = 8
  Length = 10
  Placement = pos=(78,11,32) rot=(0,0,1;0rad)
  Width = 2
FEATURE [Part::Fillet] Fillet131
  Base = -> Box250
  Edges = 2 edges r=2: [Edge6,Edge8]
FEATURE [Part::Box] Box251  label="Cube246"
  Height = 7
  Length = 10
  Placement = pos=(75,10,30) rot=(0,0,1;0rad)
  Width = 3
FEATURE [Part::Chamfer] Chamfer020
  Base = -> Box251
  Edges = 1 edges r=3: [Edge6]
FEATURE [Part::Chamfer] Chamfer021
  Base = -> Chamfer020
  Edges = 1 edges: [Edge3 r1=2 r2=4]
FEATURE [Part::Chamfer] Chamfer023
  Base = -> Chamfer021
  Edges = 1 edges: [Edge18 r1=6 r2=2]
FEATURE [Part::Chamfer] Chamfer024
  Base = -> Chamfer023
  Edges = 1 edges r=3: [Edge15]
  Placement = pos=(0,1,0) rot=(0,0,1;0rad)
FEATURE [Part::Box] Box252  label="Cube247"
  Height = 8
  Length = 10
  Placement = pos=(78,11,32) rot=(0,0,1;0rad)
  Width = 2
FEATURE [Part::Fillet] Fillet132
  Base = -> Box252
  Edges = 2 edges r=2: [Edge6,Edge8]
FEATURE [Part::Box] Box253  label="Cube248"
  Height = 7
  Length = 10
  Placement = pos=(75,10,30) rot=(0,0,1;0rad)
  Width = 3
FEATURE [Part::Chamfer] Chamfer025
  Base = -> Box253
  Edges = 1 edges r=3: [Edge6]
FEATURE [Part::Chamfer] Chamfer026
  Base = -> Chamfer025
  Edges = 1 edges: [Edge3 r1=2 r2=4]
FEATURE [Part::Chamfer] Chamfer027
  Base = -> Chamfer026
  Edges = 1 edges: [Edge18 r1=6 r2=2]
FEATURE [Part::Chamfer] Chamfer028
  Base = -> Chamfer027
  Edges = 1 edges r=3: [Edge15]
  Placement = pos=(0,1,0) rot=(0,0,1;0rad)
FEATURE [Part::MultiFuse] Fusion121
  Shapes = -> [Fillet132,Chamfer028]
FEATURE [Part::Mirroring] Part__Mirroring012  label="Fusion121 (Mirror #9)"
  Base = (0,0,0)
  Normal = (0,1,0)
  Placement = pos=(0,60,0) rot=(0,0,1;0rad)
  Source = -> Fusion121
FEATURE [Part::Cylinder] Cylinder091
  Angle = 360
  Height = 39
  Placement = pos=(81,10.5,35) rot=(-1,0,0;1.5708rad)
  Radius = 1
FEATURE [Part::Box] Box254  label="Cube249"
  Height = 7
  Length = 7
  Placement = pos=(76,8,45) rot=(0,0,1;0rad)
  Width = 3
FEATURE [Part::Box] Box255  label="Cube250"
  Height = 20
  Length = 6
  Placement = pos=(73,9,31) rot=(0,1,0;0.139626rad)
  Width = 2
FEATURE [Part::Chamfer] Chamfer029
  Base = -> Box254
  Edges = 1 edges r=5: [Edge8]
  Placement = pos=(-2,0,0) rot=(0,0,1;0rad)
FEATURE [Part::Chamfer] Chamfer030
  Base = -> Box255
  Edges = 1 edges: [Edge4 r1=5 r2=2]
FEATURE [Part::Fillet] Fillet133
  Base = -> Chamfer030
  Edges = 4 edges r=1: [Edge2,Edge9,Edge12,Edge15]
FEATURE [Part::Box] Box256  label="Cube251"
  Height = 3
  Length = 21
  Placement = pos=(59,7,49) rot=(0,0,1;0rad)
  Width = 4
FEATURE [Part::Box] Box257  label="Cube252"
  Height = 3
  Length = 25
  Placement = pos=(56,6.5,50) rot=(0,0,1;0rad)
  Width = 4.5
FEATURE [Part::Chamfer] Chamfer031
  Base = -> Box257
  Edges = 1 edges: [Edge6 r1=1 r2=18]
FEATURE [Part::Fillet] Fillet134
  Base = -> Chamfer031
  Edges = 2 edges r=1: [Edge2,Edge3]
FEATURE [Part::Fillet] Fillet135
  Base = -> Chamfer029
  Edges = 2 edges r=1: [Edge2,Edge3]
FEATURE [Part::Fillet] Fillet136
  Base = -> Fillet135
  Edges = 2 edges r=1: [Edge19,Edge20]
FEATURE [Part::Fillet] Fillet137
  Base = -> Box256
  Edges = 2 edges r=1: [Edge4,Edge8]
FEATURE [Part::Fillet] Fillet138
  Base = -> Fillet134
  Edges = 2 edges r=1.24: [Edge19,Edge21]
FEATURE [Part::Fillet] Fillet139
  Base = -> Fillet138
  Edges = 6 edges r=0.5: [Edge1,Edge8,Edge9,Edge10,Edge25,Edge27]
FEATURE [Part::MultiFuse] Fusion123
  Shapes = -> [Fillet133,Fillet136,Fillet139,Fillet137]
FEATURE [Part::Fillet] Fillet140
  Base = -> Fusion123
  Edges = 1 edges r=1: [Edge49]
FEATURE [Part::MultiFuse] Fusion124
  Shapes = -> [Fillet131,Chamfer024]
FEATURE [Part::MultiFuse] Fusion125
  Shapes = -> [Part__Mirroring012,Fusion124]
FEATURE [Part::MultiFuse] Fusion126
  Shapes = -> [Fusion125,Cylinder091]
FEATURE [Part::Box] Box258  label="Cube253"
  Height = 7
  Length = 7
  Placement = pos=(76,8,45) rot=(0,0,1;0rad)
  Width = 3
FEATURE [Part::Box] Box259  label="Cube254"
  Height = 20
  Length = 6
  Placement = pos=(73,9,31) rot=(0,1,0;0.139626rad)
  Width = 2
FEATURE [Part::Chamfer] Chamfer032
  Base = -> Box258
  Edges = 1 edges r=5: [Edge8]
  Placement = pos=(-2,0,0) rot=(0,0,1;0rad)
FEATURE [Part::Chamfer] Chamfer033
  Base = -> Box259
  Edges = 1 edges: [Edge4 r1=5 r2=2]
FEATURE [Part::Fillet] Fillet141
  Base = -> Chamfer033
  Edges = 4 edges r=1: [Edge2,Edge9,Edge12,Edge15]
FEATURE [Part::Box] Box260  label="Cube255"
  Height = 3
  Length = 21
  Placement = pos=(59,7,49) rot=(0,0,1;0rad)
  Width = 4
FEATURE [Part::Box] Box261  label="Cube256"
  Height = 3
  Length = 25
  Placement = pos=(56,6.5,50) rot=(0,0,1;0rad)
  Width = 4.5
FEATURE [Part::Chamfer] Chamfer034
  Base = -> Box261
  Edges = 1 edges: [Edge6 r1=1 r2=18]
FEATURE [Part::Fillet] Fillet142
  Base = -> Chamfer034
  Edges = 2 edges r=1: [Edge2,Edge3]
FEATURE [Part::Fillet] Fillet143
  Base = -> Chamfer032
  Edges = 2 edges r=1: [Edge2,Edge3]
FEATURE [Part::Fillet] Fillet144
  Base = -> Fillet143
  Edges = 2 edges r=1: [Edge19,Edge20]
FEATURE [Part::Fillet] Fillet145
  Base = -> Box260
  Edges = 2 edges r=1: [Edge4,Edge8]
FEATURE [Part::Fillet] Fillet146
  Base = -> Fillet142
  Edges = 2 edges r=1.24: [Edge19,Edge21]
FEATURE [Part::Fillet] Fillet147
  Base = -> Fillet146
  Edges = 6 edges r=0.5: [Edge1,Edge8,Edge9,Edge10,Edge25,Edge27]
FEATURE [Part::MultiFuse] Fusion127
  Shapes = -> [Fillet141,Fillet144,Fillet147,Fillet145]
FEATURE [Part::Fillet] Fillet148
  Base = -> Fusion127
  Edges = 1 edges r=1: [Edge49]
FEATURE [Part::Mirroring] Part__Mirroring013  label="Fillet148 (Mirror #10)"
  Base = (0,0,0)
  Normal = (0,1,0)
  Placement = pos=(0,60,0) rot=(0,0,1;0rad)
  Source = -> Fillet148
FEATURE [Part::MultiFuse] Fusion128
  Shapes = -> [Part__Mirroring013,Fillet140]
FEATURE [Part::MultiFuse] Fusion129
  Shapes = -> [Fillet126,Fusion126,Fillet120]
FEATURE [Part::Box] Box262  label="Cube257"
  Height = 10
  Length = 38
  Placement = pos=(45,11,30) rot=(0,0,1;0rad)
  Width = 38
FEATURE [Part::Box] Box263  label="Cube258"
  Height = 45
  Length = 13
  Placement = pos=(75,11,30) rot=(0,0,1;0rad)
  Width = 38
FEATURE [Part::Chamfer] Chamfer035
  Base = -> Box262
  Edges = 2 edges: [Edge2 r1=2 r2=12,Edge6 r1=2 r2=12]
FEATURE [Part::Fillet] Fillet149
  Base = -> Chamfer035
  Edges = 3 edges r=3: [Edge3,Edge13,Edge17]
FEATURE [Part::Fillet] Fillet150
  Base = -> Fillet149
  Edges = 1 edges r=5: [Edge3]
FEATURE [Part::Fillet] Fillet151
  Base = -> Fillet150
  Edges = 6 edges r=2: [Edge7,Edge9,Edge11,Edge18,Edge20,Edge22]
FEATURE [Part::Fillet] Fillet152
  Base = -> Fillet151
  Edges = 2 edges r=20: [Edge23,Edge49]
FEATURE [Part::Chamfer] Chamfer036
  Base = -> Box263
  Edges = 1 edges: [Edge2 r1=20 r2=5]
FEATURE [Part::Chamfer] Chamfer037
  Base = -> Chamfer036
  Edges = 1 edges: [Edge3 r1=15 r2=3]
FEATURE [Part::Fillet] Fillet153
  Base = -> Chamfer037
  Edges = 4 edges r=3: [Edge10,Edge12,Edge17,Edge18]
FEATURE [Part::Fillet] Fillet154
  Base = -> Fillet153
  Edges = 2 edges r=20: [Edge12,Edge16]
FEATURE [Part::Fillet] Fillet155
  Base = -> Fillet154
  Edges = 10 edges r=2: [Edge1,Edge2,Edge4,Edge6,Edge8,Edge15,Edge17,Edge21,Edge25,Edge29]
FEATURE [Part::Box] Box264  label="Cube259"
  Height = 48
  Length = 7
  Placement = pos=(69,12,30) rot=(0,1,0;0.10472rad)
  Width = 36
FEATURE [Part::Box] Box265  label="Cube260"
  Height = 50
  Length = 16
  Placement = pos=(75,0,30) rot=(-0.683576,-0.016559,0.729691;0.239394rad)
  Width = 8
FEATURE [Part::Box] Box266  label="Cube261"
  Height = 50
  Length = 16
  Placement = pos=(75,0,30) rot=(-0.683576,-0.016559,0.729691;0.239394rad)
  Width = 8
FEATURE [Part::Mirroring] Part__Mirroring014  label="Cube241 (Mirror #7)001"
  Base = (0,0,0)
  Normal = (0,1,0)
  Placement = pos=(0,60,0) rot=(0,0,1;0rad)
  Source = -> Box266
FEATURE [Part::MultiFuse] Fusion130
  Shapes = -> [Part__Mirroring014,Box265]
FEATURE [Part::Cut] Cut149
  Base = -> Fillet155
  Tool = -> Fusion130
FEATURE [Part::Fillet] Fillet156
  Base = -> Cut149
  Edges = 4 edges r=1.6: [Edge19,Edge23,Edge40,Edge49]
FEATURE [Part::Chamfer] Chamfer038
  Base = -> Box264
  Edges = 2 edges: [Edge10 r1=40 r2=4,Edge12 r1=40 r2=4]
FEATURE [Part::Chamfer] Chamfer039
  Base = -> Chamfer038
  Edges = 2 edges: [Edge11 r1=4 r2=7,Edge18 r1=4 r2=7]
FEATURE [Part::Fillet] Fillet157
  Base = -> Chamfer039
  Edges = 2 edges r=10: [Edge18,Edge24]
  Placement = pos=(-0.75,0,0) rot=(0,0,1;0rad)
FEATURE [Part::Cut] Cut150
  Base = -> Fillet156
  Tool = -> Fillet157
FEATURE [Part::Fillet] Fillet158
  Base = -> Cut150
  Edges = 2 edges r=2.5: [Edge93,Edge106]
FEATURE [Part::Box] Box267  label="Cube262"
  Height = 8
  Length = 10
  Placement = pos=(78,11,32) rot=(0,0,1;0rad)
  Width = 2
FEATURE [Part::Fillet] Fillet159
  Base = -> Box267
  Edges = 2 edges r=2: [Edge6,Edge8]
FEATURE [Part::Box] Box268  label="Cube263"
  Height = 7
  Length = 10
  Placement = pos=(75,10,30) rot=(0,0,1;0rad)
  Width = 3
FEATURE [Part::Chamfer] Chamfer040
  Base = -> Box268
  Edges = 1 edges r=3: [Edge6]
FEATURE [Part::Chamfer] Chamfer041
  Base = -> Chamfer040
  Edges = 1 edges: [Edge3 r1=2 r2=4]
FEATURE [Part::Chamfer] Chamfer042
  Base = -> Chamfer041
  Edges = 1 edges: [Edge18 r1=6 r2=2]
FEATURE [Part::Chamfer] Chamfer043
  Base = -> Chamfer042
  Edges = 1 edges r=3: [Edge15]
  Placement = pos=(0,1,0) rot=(0,0,1;0rad)
FEATURE [Part::Box] Box269  label="Cube264"
  Height = 8
  Length = 10
  Placement = pos=(78,11,32) rot=(0,0,1;0rad)
  Width = 2
FEATURE [Part::Fillet] Fillet160
  Base = -> Box269
  Edges = 2 edges r=2: [Edge6,Edge8]
FEATURE [Part::Box] Box270  label="Cube265"
  Height = 7
  Length = 10
  Placement = pos=(75,10,30) rot=(0,0,1;0rad)
  Width = 3
FEATURE [Part::Chamfer] Chamfer044
  Base = -> Box270
  Edges = 1 edges r=3: [Edge6]
FEATURE [Part::Chamfer] Chamfer045
  Base = -> Chamfer044
  Edges = 1 edges: [Edge3 r1=2 r2=4]
FEATURE [Part::Chamfer] Chamfer046
  Base = -> Chamfer045
  Edges = 1 edges: [Edge18 r1=6 r2=2]
FEATURE [Part::Chamfer] Chamfer047
  Base = -> Chamfer046
  Edges = 1 edges r=3: [Edge15]
  Placement = pos=(0,1,0) rot=(0,0,1;0rad)
FEATURE [Part::MultiFuse] Fusion131
  Shapes = -> [Fillet160,Chamfer047]
FEATURE [Part::Mirroring] Part__Mirroring015  label="Fusion121 (Mirror #9)001"
  Base = (0,0,0)
  Normal = (0,1,0)
  Placement = pos=(0,60,0) rot=(0,0,1;0rad)
  Source = -> Fusion131
FEATURE [Part::Cylinder] Cylinder092
  Angle = 360
  Height = 39
  Placement = pos=(81,10.5,35) rot=(-1,0,0;1.5708rad)
  Radius = 1
FEATURE [Part::MultiFuse] Fusion132
  Shapes = -> [Fillet159,Chamfer043]
FEATURE [Part::MultiFuse] Fusion133
  Shapes = -> [Part__Mirroring015,Fusion132]
FEATURE [Part::MultiFuse] Fusion134
  Shapes = -> [Fusion133,Cylinder092]
FEATURE [Part::MultiFuse] Fusion135  label="seat-right"
  Placement = pos=(-5,108,0) rot=(0,0,1;0rad)
  Shapes = -> [Fillet158,Fusion134,Fillet152]
FEATURE [Part::MultiFuse] Fusion136
  Shapes = -> [Fusion129,Fillet130]
FEATURE [Part::MultiFuse] Fusion137  label="seat-left"
  Placement = pos=(-2,0,0) rot=(0,0,1;0rad)
  Shapes = -> [Fusion136,Fusion128]
FEATURE [Part::Cylinder] Cylinder093  label="steering-rod-METAL"
  Angle = 360
  Height = 59
  Placement = pos=(18.5,138,3) rot=(0,1,0;0.261799rad)
  Radius = 1.6
FEATURE [Part::Torus] Torus
  Angle1 = -180
  Angle2 = 180
  Angle3 = 360
  Placement = pos=(34,138,61) rot=(0,1,0;0.261799rad)
  Radius1 = 17
  Radius2 = 1
FEATURE [Part::Cylinder] Cylinder094
  Angle = 360
  Height = 55
  Placement = pos=(18.5,138,3) rot=(0,1,0;0.261799rad)
  Radius = 4
FEATURE [Part::Box] Box271  label="Cube266"
  Height = 10
  Length = 14
  Placement = pos=(17,134,35) rot=(0,1,0;0.261799rad)
  Width = 8
FEATURE [Part::Cylinder] Cylinder095
  Angle = 360
  Height = 32
  Placement = pos=(18.5,138,3) rot=(0,1,0;0.261799rad)
  Radius = 4
FEATURE [Part::Cut] Cut151
  Base = -> Cylinder094
  Tool = -> Cylinder095
FEATURE [Part::Fillet] Fillet161
  Base = -> Box271
  Edges = 4 edges r=1: [Edge9,Edge10,Edge11,Edge12]
FEATURE [Part::Fillet] Fillet162
  Base = -> Fillet161
  Edges = 2 edges r=2: [Edge9,Edge24]
FEATURE [Part::Box] Box272  label="Cube267"
  Height = 4
  Length = 8
  Placement = pos=(27.75,134,53) rot=(0,1,0;0.261799rad)
  Width = 12
FEATURE [Part::Chamfer] Chamfer048
  Base = -> Box272
  Edges = 1 edges: [Edge11 r1=1 r2=5]
FEATURE [Part::Fillet] Fillet163
  Base = -> Chamfer048
  Edges = 12 edges r=0.5: [Edge1,Edge3,Edge4,Edge5,Edge6,Edge7,Edge8,Edge11,Edge12,Edge13,Edge14,Edge15]
FEATURE [Part::MultiFuse] Fusion138
  Shapes = -> [Cut151,Fillet162,Fillet163]
FEATURE [Part::Cylinder] Cylinder096
  Angle = 360
  Height = 10
  Placement = pos=(30.5,136,54.8) rot=(-1,0,0;1.5708rad)
  Radius = 0.8
FEATURE [Part::Cylinder] Cylinder097
  Angle = 360
  Height = 10
  Placement = pos=(34,136,53.9) rot=(-1,0,0;1.5708rad)
  Radius = 0.8
FEATURE [Part::MultiFuse] Fusion139
  Shapes = -> [Cylinder096,Cylinder097]
FEATURE [Part::Cut] Cut152
  Base = -> Fusion138
  Tool = -> Fusion139
FEATURE [Part::Cylinder] Cylinder098
  Angle = 360
  Height = 62
  Placement = pos=(18.5,138,3) rot=(0,1,0;0.261799rad)
  Radius = 1.6
FEATURE [Part::Cut] Cut153
  Base = -> Cut152
  Tool = -> Cylinder098
FEATURE [Part::Cylinder] Cylinder099
  Angle = 360
  Height = 59.5
  Placement = pos=(18.5,138,3) rot=(0,1,0;0.261799rad)
  Radius = 1.6
FEATURE [Part::Cylinder] Cylinder100
  Angle = 360
  Height = 60
  Placement = pos=(18.5,138,3) rot=(0,1,0;0.261799rad)
  Radius = 4
FEATURE [Part::Cylinder] Cylinder101
  Angle = 360
  Height = 56
  Placement = pos=(18.5,138,3) rot=(0,1,0;0.261799rad)
  Radius = 4
FEATURE [Part::Cut] Cut154
  Base = -> Cylinder100
  Tool = -> Cylinder101
FEATURE [Part::Box] Box273  label="Cube268"
  Height = 3
  Length = 3.5
  Placement = pos=(33.5,121,58) rot=(0,1,0;0.261799rad)
  Width = 34
FEATURE [Part::Box] Box274  label="Cube269"
  Height = 3
  Length = 5
  Placement = pos=(33,123,58) rot=(0,1,0;0.261799rad)
  Width = 30
FEATURE [Part::Chamfer] Chamfer050
  Base = -> Box274
  Edges = 2 edges: [Edge9 r1=2 r2=10,Edge11 r1=2 r2=10]
  Placement = pos=(0,0,2) rot=(0,0,1;0rad)
FEATURE [Part::Box] Box275  label="Cube270"
  Height = 3
  Length = 5
  Placement = pos=(33.5,121,58) rot=(0,1,0;0.261799rad)
  Width = 34
FEATURE [Part::Box] Box276  label="Cube271"
  Height = 3
  Length = 6
  Placement = pos=(32,122,59) rot=(0,1,0;0.261799rad)
  Width = 32
FEATURE [Part::Chamfer] Chamfer051
  Base = -> Box276
  Edges = 2 edges: [Edge9 r1=2.99 r2=10,Edge11 r1=2.99 r2=10]
  Placement = pos=(1,0,0) rot=(0,0,1;0rad)
FEATURE [Part::Cut] Cut155
  Base = -> Box275
  Placement = pos=(-1,0,-0.75) rot=(0,0,1;0rad)
  Tool = -> Chamfer051
FEATURE [Part::Cut] Cut156
  Base = -> Box273
  Tool = -> Chamfer050
FEATURE [Part::Cut] Cut157
  Base = -> Cut156
  Tool = -> Cut155
FEATURE [Part::MultiFuse] Fusion140
  Shapes = -> [Cut154,Cut157]
FEATURE [Part::Fillet] Fillet164
  Base = -> Fusion140
  Edges = 2 edges r=3: [Edge5,Edge10]
FEATURE [Part::Fillet] Fillet165
  Base = -> Fillet164
  Edges = 8 edges r=5: [Edge14,Edge27,Edge30,Edge41,Edge43,Edge50,Edge52,Edge58]
FEATURE [Part::Cut] Cut158
  Base = -> Fillet165
  Tool = -> Cylinder099
FEATURE [Part::Fillet] Fillet166
  Base = -> Cut158
  Edges = 1 edges r=1: [Edge18]
FEATURE [Part::Chamfer] Chamfer052
  Base = -> Fillet166
  Edges = 4 edges r=0.79: [Edge26,Edge47,Edge58,Edge74]
FEATURE [Part::MultiFuse] Fusion141  label="steering-wheel"
  Shapes = -> [Torus,Chamfer052]
FEATURE [Part::Cut] Cut159
  Base = -> Cut130
  Tool = -> Fillet116
FEATURE [Part::Box] Box277  label="Cube272"
  Height = 17
  Length = 100
  Placement = pos=(50,121,4) rot=(0,0,1;0rad)
  Width = 20
FEATURE [Part::Box] Box278  label="Cube273"
  Height = 36
  Length = 42
  Placement = pos=(91,115,4) rot=(0,0,1;0rad)
  Width = 14
FEATURE [Part::Box] Box279  label="Cube274"
  Height = 36
  Length = 57
  Placement = pos=(83,110,4) rot=(0,0,1;0rad)
  Width = 16
FEATURE [Part::Box] Box280  label="Cube275"
  Height = 2
  Length = 28
  Placement = pos=(45,121,21) rot=(0,0,1;0rad)
  Width = 34
FEATURE [Part::Cylinder] Cylinder102
  Angle = 360
  Height = 184
  Placement = pos=(98,176,-23) rot=(1,0,0;1.5708rad)
  Radius = 53
FEATURE [Part::Cylinder] Cylinder103
  Angle = 360
  Height = 18
  Placement = pos=(47,153,4) rot=(0,0,1;0rad)
  Radius = 2
FEATURE [Part::Cylinder] Cylinder104
  Angle = 360
  Height = 18
  Placement = pos=(47,123,4) rot=(0,0,1;0rad)
  Radius = 2
FEATURE [Part::Cylinder] Cylinder105
  Angle = 360
  Height = 17
  Placement = pos=(47,153,5) rot=(0,0,1;0rad)
  Radius = 2
FEATURE [Part::Cylinder] Cylinder106
  Angle = 360
  Height = 17
  Placement = pos=(47,123,5) rot=(0,0,1;0rad)
  Radius = 2
FEATURE [Part::MultiFuse] Fusion143
  Placement = pos=(0,0,-2) rot=(0,0,1;0rad)
  Shapes = -> [Cylinder105,Cylinder106]
FEATURE [Part::Cylinder] Cylinder107
  Angle = 360
  Height = 17
  Placement = pos=(47,153,5) rot=(0,0,1;0rad)
  Radius = 2
FEATURE [Part::Cylinder] Cylinder108
  Angle = 360
  Height = 17
  Placement = pos=(47,123,5) rot=(0,0,1;0rad)
  Radius = 2
FEATURE [Part::MultiFuse] Fusion144
  Placement = pos=(0,-108,-2) rot=(0,0,1;0rad)
  Shapes = -> [Cylinder107,Cylinder108]
FEATURE [Part::MultiFuse] Fusion145
  Shapes = -> [Cylinder103,Cylinder104,Box280]
FEATURE [Part::Cut] Cut162  label="seat-support-left"
  Base = -> Fusion145
  Placement = pos=(0,-108,0) rot=(0,0,1;0rad)
  Tool = -> Cylinder102
FEATURE [Part::Box] Box281  label="Cube276"
  Height = 2
  Length = 28
  Placement = pos=(45,121,21) rot=(0,0,1;0rad)
  Width = 34
FEATURE [Part::Cylinder] Cylinder109
  Angle = 360
  Height = 184
  Placement = pos=(98,176,-23) rot=(1,0,0;1.5708rad)
  Radius = 53
FEATURE [Part::Cylinder] Cylinder110
  Angle = 360
  Height = 18
  Placement = pos=(47,153,4) rot=(0,0,1;0rad)
  Radius = 2
FEATURE [Part::Cylinder] Cylinder111
  Angle = 360
  Height = 18
  Placement = pos=(47,123,4) rot=(0,0,1;0rad)
  Radius = 2
FEATURE [Part::MultiFuse] Fusion146
  Shapes = -> [Cylinder110,Cylinder111,Box281]
FEATURE [Part::Cut] Cut163  label="seat-support-right"
  Base = -> Fusion146
  Tool = -> Cylinder109
FEATURE [Part::Cylinder] Cylinder112  label="shift-rod-METAL"
  Angle = 360
  Height = 45
  Placement = pos=(42.5,115,3) rot=(0,0,1;0rad)
  Radius = 1
FEATURE [Part::Cylinder] Cylinder113  label="cylinder"
  Angle = 360
  Height = 2
  Placement = pos=(42.5,115,5) rot=(0,0,1;0rad)
  Radius = 2.5
FEATURE [Part::Cylinder] Cylinder114  label="cylinder001"
  Angle = 360
  Height = 3
  Placement = pos=(42.5,115,4) rot=(0,0,1;0rad)
  Radius = 1
FEATURE [Part::Fillet] Fillet167
  Base = -> Cylinder113
  Edges = 1 edges r=1: [Edge1]
FEATURE [Part::Box] Box286  label="Cube281"
  Height = 3
  Length = 6
  Placement = pos=(38,113,48) rot=(0,0,1;0rad)
  Width = 4
FEATURE [Part::Fillet] Fillet168
  Base = -> Box286
  Edges = 2 edges r=1: [Edge5,Edge7]
FEATURE [Part::Fillet] Fillet169
  Base = -> Fillet168
  Edges = 2 edges r=1.5: [Edge17,Edge18]
FEATURE [Part::Cylinder] Cylinder115  label="cylinder002"
  Angle = 360
  Height = 52
  Placement = pos=(42.5,115,3) rot=(0,0,1;0rad)
  Radius = 1
FEATURE [Part::Cylinder] Cylinder116  label="cylinder003"
  Angle = 360
  Height = 2
  Placement = pos=(39.5,115,51) rot=(0,-1,0;0.139626rad)
  Radius = 0.3
FEATURE [Part::Cylinder] Cylinder117  label="cylinder004"
  Angle = 360
  Height = 0.5
  Placement = pos=(39.5,115,51) rot=(0,0,1;0rad)
  Radius = 1
FEATURE [Part::Fillet] Fillet170
  Base = -> Cylinder117
  Edges = 1 edges r=0.3: [Edge1]
FEATURE [Part::MultiFuse] Fusion150
  Shapes = -> [Cylinder116,Fillet170,Fillet169]
FEATURE [Part::Cut] Cut167  label="gear-lever-splitter"
  Base = -> Fusion150
  Placement = pos=(0,0,-7) rot=(0,0,1;0rad)
  Tool = -> Cylinder115
FEATURE [Part::Cylinder] Cylinder118  label="cylinder005"
  Angle = 360
  Height = 52
  Placement = pos=(42.5,115,3) rot=(0,0,1;0rad)
  Radius = 1
FEATURE [Part::Cylinder] Cylinder119  label="cylinder006"
  Angle = 360
  Height = 2
  Placement = pos=(42.5,115,53.5) rot=(0,0,1;0rad)
  Radius = 2
FEATURE [Part::Fillet] Fillet171
  Base = -> Cylinder119
  Edges = 2 edges r=0.75: [Edge1,Edge3]
FEATURE [Part::Cut] Cut168  label="gear-lever-knob"
  Base = -> Fillet171
  Placement = pos=(0,0,-6) rot=(0,0,1;0rad)
  Tool = -> Cylinder118
FEATURE [Part::Box] Box287  label="Cube282"
  Height = 22
  Length = 10
  Placement = pos=(4,7,35) rot=(0,0,1;0rad)
  Width = 154
FEATURE [Part::Box] Box288  label="Cube283"
  Height = 22
  Length = 10
  Placement = pos=(14,7,35) rot=(0,0,1;0rad)
  Width = 154
FEATURE [Part::Chamfer] Chamfer055
  Base = -> Box288
  Edges = 1 edges: [Edge6 r1=15 r2=8]
FEATURE [Part::Chamfer] Chamfer056
  Base = -> Chamfer055
  Edges = 1 edges r=5: [Edge3]
FEATURE [Part::MultiFuse] Fusion151
  Shapes = -> [Box287,Chamfer056]
FEATURE [Part::Fillet] Fillet172
  Base = -> Fusion151
  Edges = 4 edges r=2: [Edge2,Edge3,Edge6,Edge9]
FEATURE [Part::Cut] Cut169  label="steering-hub"
  Base = -> Cut153
  Tool = -> Fillet172
FEATURE [Part::Cylinder] Cylinder120  label="cylinder007"
  Angle = 360
  Height = 59
  Placement = pos=(18.5,138,3) rot=(0,1,0;0.261799rad)
  Radius = 1.6
FEATURE [Part::Box] Box289  label="Cube284"
  Height = 13.5
  Length = 1
  Placement = pos=(22.75,7,43) rot=(0,-1,0;0.488692rad)
  Width = 154
FEATURE [Part::Cut] Cut171
  Base = -> Cut159
  Tool = -> Box289
FEATURE [Part::Chamfer] Chamfer057
  Base = -> Cut171
  Edges = 3 edges r=0.6: [Edge43,Edge53,Edge94]
FEATURE [Part::Box] Box290  label="Cube285"
  Height = 13.5
  Length = 1
  Placement = pos=(22.75,49,43) rot=(0,-1,0;0.488692rad)
  Width = 6
FEATURE [Part::Box] Box291  label="Cube286"
  Height = 13.5
  Length = 1
  Placement = pos=(22.75,113,43) rot=(0,-1,0;0.488692rad)
  Width = 6
FEATURE [Part::Fillet] Fillet173
  Base = -> Box291
  Edges = 2 edges r=0.99: [Edge6,Edge8]
FEATURE [Part::Fillet] Fillet174
  Base = -> Box290
  Edges = 2 edges r=0.99: [Edge6,Edge8]
FEATURE [Part::Box] Box292  label="Cube287"
  Height = 13.5
  Length = 0.5
  Placement = pos=(22.75,120,43) rot=(0,-1,0;1.5708rad)
  Width = 40
FEATURE [Part::Cylinder] Cylinder121  label="Cylinder112"
  Angle = 360
  Height = 1
  Placement = pos=(16,153,43) rot=(0,0,1;0rad)
  Radius = 5.5
FEATURE [Part::Cylinder] Cylinder122  label="Cylinder113"
  Angle = 360
  Height = 1
  Placement = pos=(16,134,43) rot=(0,0,1;0rad)
  Radius = 5.5
FEATURE [Part::Cylinder] Cylinder123  label="Cylinder114"
  Angle = 360
  Height = 1
  Placement = pos=(13,143.5,43) rot=(0,0,1;0rad)
  Radius = 3
FEATURE [Part::Cylinder] Cylinder124  label="Cylinder115"
  Angle = 360
  Height = 1
  Placement = pos=(11,122,43) rot=(0,0,1;0rad)
  Radius = 1
FEATURE [Part::Cylinder] Cylinder125  label="Cylinder116"
  Angle = 360
  Height = 1
  Placement = pos=(11,124.5,43) rot=(0,0,1;0rad)
  Radius = 1
FEATURE [Part::Cylinder] Cylinder126  label="Cylinder143"
  Angle = 360
  Height = 1
  Placement = pos=(14,122,43) rot=(0,0,1;0rad)
  Radius = 1
FEATURE [Part::Cylinder] Cylinder127  label="Cylinder144"
  Angle = 360
  Height = 1
  Placement = pos=(14,124.5,43) rot=(0,0,1;0rad)
  Radius = 1
FEATURE [Part::Cylinder] Cylinder128  label="Cylinder145"
  Angle = 360
  Height = 1
  Placement = pos=(14,127,43) rot=(0,0,1;0rad)
  Radius = 1
FEATURE [Part::Cylinder] Cylinder129  label="Cylinder146"
  Angle = 360
  Height = 1
  Placement = pos=(17,122,43) rot=(0,0,1;0rad)
  Radius = 1
FEATURE [Part::Cylinder] Cylinder130  label="Cylinder147"
  Angle = 360
  Height = 1
  Placement = pos=(17,124.5,43) rot=(0,0,1;0rad)
  Radius = 1
FEATURE [Part::Cylinder] Cylinder131  label="Cylinder148"
  Angle = 360
  Height = 1
  Placement = pos=(17,127,43) rot=(0,0,1;0rad)
  Radius = 1
FEATURE [Part::Box] Box293  label="Cube288"
  Height = 1
  Length = 2
  Placement = pos=(19,121.25,43) rot=(0,0,1;0rad)
  Width = 1.5
FEATURE [Part::Box] Box294  label="Cube289"
  Height = 1
  Length = 2
  Placement = pos=(19,123.75,43) rot=(0,0,1;0rad)
  Width = 1.5
FEATURE [Part::Box] Box295  label="Cube290"
  Height = 1
  Length = 2
  Placement = pos=(19,126.25,43) rot=(0,0,1;0rad)
  Width = 1.5
FEATURE [Part::Box] Box296  label="Cube291"
  Height = 1
  Length = 1
  Placement = pos=(20,121.25,44) rot=(0,0,1;0rad)
  Width = 1.5
FEATURE [Part::Box] Box297  label="Cube292"
  Height = 1
  Length = 1
  Placement = pos=(20,123.75,44) rot=(0,0,1;0rad)
  Width = 1.5
FEATURE [Part::Box] Box298  label="Cube293"
  Height = 1
  Length = 1
  Placement = pos=(20,126.25,44) rot=(0,0,1;0rad)
  Width = 1.5
FEATURE [Part::Cylinder] Cylinder132  label="Cylinder149"
  Angle = 360
  Height = 1
  Placement = pos=(16,153,43) rot=(0,0,1;0rad)
  Radius = 4.5
FEATURE [Part::Cylinder] Cylinder133  label="Cylinder150"
  Angle = 360
  Height = 1
  Placement = pos=(16,134,43) rot=(0,0,1;0rad)
  Radius = 4.5
FEATURE [Part::Cylinder] Cylinder134  label="Cylinder151"
  Angle = 360
  Height = 1
  Placement = pos=(13,143.5,43) rot=(0,0,1;0rad)
  Radius = 2.5
FEATURE [Part::Cut] Cut172
  Base = -> Cylinder121
  Tool = -> Cylinder132
FEATURE [Part::Cut] Cut173
  Base = -> Cylinder122
  Tool = -> Cylinder133
FEATURE [Part::Cut] Cut174
  Base = -> Cylinder123
  Tool = -> Cylinder134
FEATURE [Part::MultiFuse] Fusion152
  Shapes = -> [Cut172,Cut174,Cut173]
FEATURE [Part::Fillet] Fillet175
  Base = -> Fusion152
  Edges = 2 edges r=0.5: [Edge1,Edge7]
FEATURE [Part::Fillet] Fillet176
  Base = -> Fillet175
  Edges = 1 edges r=0.3: [Edge17]
FEATURE [Part::Chamfer] Chamfer058
  Base = -> Fillet176
  Edges = 2 edges r=0.49: [Edge15,Edge23]
FEATURE [Part::Chamfer] Chamfer059
  Base = -> Chamfer058
  Edges = 1 edges r=0.19: [Edge27]
FEATURE [Part::MultiFuse] Fusion153
  Shapes = -> [Cylinder129,Cylinder127,Cylinder128,Cylinder125,Cylinder124,Cylinder130,Cylinder126,Cylinder131]
FEATURE [Part::MultiFuse] Fusion154
  Shapes = -> [Box296,Box297,Box298]
FEATURE [Part::MultiFuse] Fusion155
  Shapes = -> [Box293,Box294,Box295]
FEATURE [Part::Chamfer] Chamfer060
  Base = -> Fusion154
  Edges = 3 edges r=0.8: [Edge2,Edge14,Edge26]
  Placement = pos=(0,0,-0.3) rot=(0,0,1;0rad)
FEATURE [Part::MultiFuse] Fusion156  label="dashboard-instruments"
  Placement = pos=(-26,0,43) rot=(0,1,0;1.0821rad)
  Shapes = -> [Box292,Fusion155,Chamfer060,Fusion153,Chamfer059]
FEATURE [Part::MultiFuse] Fusion157  label="dashboard"
  Shapes = -> [Chamfer057,Fillet173,Fillet174]
FEATURE [Part::Box] Box299  label="Cube294"
  Height = 1
  Length = 4.5
  Placement = pos=(78.5,70,48) rot=(0,0,1;0rad)
  Width = 28
FEATURE [Part::Box] Box300  label="Cube295"
  Height = 2
  Length = 8
  Placement = pos=(75,78,48) rot=(0,0,1;0rad)
  Width = 12
FEATURE [Part::Box] Box301  label="Cube296"
  Height = 2
  Length = 6
  Placement = pos=(69,81,48) rot=(0,0,1;0rad)
  Width = 6
FEATURE [Part::MultiFuse] Fusion158
  Shapes = -> [Box300,Box301]
FEATURE [Part::Fillet] Fillet177
  Base = -> Fusion158
  Edges = 2 edges r=2: [Edge18,Edge21]
FEATURE [Part::Fillet] Fillet178
  Base = -> Fillet177
  Edges = 4 edges r=1.499: [Edge3,Edge17,Edge29,Edge30]
FEATURE [Part::MultiFuse] Fusion159
  Shapes = -> [Box223,Fillet178,Box299]
FEATURE [Part::Cut] Cut175  label="central-tunnel"
  Base = -> Fillet111
  Tool = -> Fusion159
FEATURE [Part::MultiFuse] Fusion160
  Shapes = -> [Box279,Box278]
FEATURE [Part::Cut] Cut176
  Base = -> Part__Mirroring009
  Tool = -> Box277
FEATURE [Part::Cut] Cut177
  Base = -> Cut176
  Tool = -> Fusion160
FEATURE [Part::Cut] Cut178
  Base = -> Cut177
  Tool = -> Fusion143
FEATURE [Part::MultiFuse] Fusion161
  Shapes = -> [Cut178,Fillet167]
FEATURE [Part::Cut] Cut179
  Base = -> Fusion161
  Tool = -> Cylinder114
FEATURE [Part::Cut] Cut180  label="right-panel"
  Base = -> Cut179
  Tool = -> Cylinder120
FEATURE [Part::Box] Box302  label="Cube297"
  Height = 4
  Length = 14
  Placement = pos=(91,52,26) rot=(0,0,1;0rad)
  Width = 10.5
FEATURE [Part::MultiFuse] Fusion162
  Shapes = -> [Box237,Box302]
FEATURE [Part::Cut] Cut181
  Base = -> Cut140
  Tool = -> Fusion162
FEATURE [Part::Cut] Cut182  label="left-panel"
  Base = -> Cut181
  Tool = -> Fusion144
FEATURE [Part::Box] Box303  label="Cube298"
  Height = 6
  Length = 24
  Placement = pos=(47,123,24) rot=(0,0,1;0rad)
  Width = 30
FEATURE [Part::Box] Box304  label="Cube299"
  Height = 6
  Length = 24
  Placement = pos=(47,125,23) rot=(0,0,1;0rad)
  Width = 26
FEATURE [Part::Box] Box305  label="Cube300"
  Height = 6
  Length = 24
  Placement = pos=(47,124.5,23.2) rot=(0,0,1;0rad)
  Width = 27
FEATURE [Part::Box] Box306  label="Cube301"
  Height = 6
  Length = 24
  Placement = pos=(47,127,24) rot=(0,0,1;0rad)
  Width = 22
FEATURE [Part::Cut] Cut183
  Base = -> Box304
  Tool = -> Box306
FEATURE [Part::Cylinder] Cylinder135  label="Cylinder152"
  Angle = 180
  Height = 24
  Placement = pos=(47,124,25.5) rot=(0,1,0;1.5708rad)
  Radius = 1.5
FEATURE [Part::Cut] Cut184
  Base = -> Box303
  Tool = -> Box305
FEATURE [Part::Cylinder] Cylinder136  label="Cylinder153"
  Angle = 360
  Height = 24
  Placement = pos=(47,152,25.5) rot=(0,1,0;1.5708rad)
  Radius = 1.5
FEATURE [Part::Cylinder] Cylinder137  label="Cylinder154"
  Angle = 360
  Height = 24
  Placement = pos=(47,124,25.5) rot=(0,1,0;1.5708rad)
  Radius = 1.5
FEATURE [Part::Cylinder] Cylinder138  label="Cylinder155"
  Angle = 180
  Height = 24
  Placement = pos=(47,152,25.5) rot=(0.707107,0,0.707107;3.14159rad)
  Radius = 1.5
FEATURE [Part::MultiFuse] Fusion163
  Shapes = -> [Cylinder135,Cylinder138]
FEATURE [Part::MultiFuse] Fusion164  label="seat-support-slider-upper-left"
  Shapes = -> [Cut184,Fusion163]
FEATURE [Part::MultiFuse] Fusion165
  Shapes = -> [Cylinder137,Cylinder136]
FEATURE [Part::Cut] Cut185
  Base = -> Cut183
  Tool = -> Fusion165
FEATURE [Part::Fillet] Fillet179  label="seat-support-slider-lower-left"
  Base = -> Cut185
  Edges = 4 edges r=1: [Edge25,Edge27,Edge33,Edge35]
FEATURE [Part::Box] Box307  label="Cube302"
  Height = 6
  Length = 24
  Placement = pos=(47,123,24) rot=(0,0,1;0rad)
  Width = 30
FEATURE [Part::Box] Box308  label="Cube303"
  Height = 6
  Length = 24
  Placement = pos=(47,125,23) rot=(0,0,1;0rad)
  Width = 26
FEATURE [Part::Box] Box309  label="Cube304"
  Height = 6
  Length = 24
  Placement = pos=(47,124.5,23.2) rot=(0,0,1;0rad)
  Width = 27
FEATURE [Part::Box] Box310  label="Cube305"
  Height = 6
  Length = 24
  Placement = pos=(47,127,24) rot=(0,0,1;0rad)
  Width = 22
FEATURE [Part::Cut] Cut186
  Base = -> Box308
  Tool = -> Box310
FEATURE [Part::Cylinder] Cylinder139  label="Cylinder156"
  Angle = 180
  Height = 24
  Placement = pos=(47,124,25.5) rot=(0,1,0;1.5708rad)
  Radius = 1.5
FEATURE [Part::Cut] Cut187
  Base = -> Box307
  Tool = -> Box309
FEATURE [Part::Cylinder] Cylinder140  label="Cylinder157"
  Angle = 360
  Height = 24
  Placement = pos=(47,152,25.5) rot=(0,1,0;1.5708rad)
  Radius = 1.5
FEATURE [Part::Cylinder] Cylinder141  label="Cylinder158"
  Angle = 360
  Height = 24
  Placement = pos=(47,124,25.5) rot=(0,1,0;1.5708rad)
  Radius = 1.5
FEATURE [Part::Cylinder] Cylinder142  label="Cylinder159"
  Angle = 180
  Height = 24
  Placement = pos=(47,152,25.5) rot=(0.707107,0,0.707107;3.14159rad)
  Radius = 1.5
FEATURE [Part::MultiFuse] Fusion166
  Shapes = -> [Cylinder139,Cylinder142]
FEATURE [Part::MultiFuse] Fusion167  label="seat-support-slider-upper-right"
  Placement = pos=(0,-108,0) rot=(0,0,1;0rad)
  Shapes = -> [Cut187,Fusion166]
FEATURE [Part::MultiFuse] Fusion168
  Shapes = -> [Cylinder141,Cylinder140]
FEATURE [Part::Cut] Cut188
  Base = -> Cut186
  Tool = -> Fusion168
FEATURE [Part::Fillet] Fillet180  label="seat-support-slider-lower-right"
  Base = -> Cut188
  Edges = 4 edges r=1: [Edge25,Edge27,Edge33,Edge35]
  Placement = pos=(0,-108,0) rot=(0,0,1;0rad)
FEATURE [Part::Box] Box311  label="Cube306"
  Height = 35
  Length = 55
  Placement = pos=(82,10,29) rot=(0,0,1;0rad)
  Width = 148
FEATURE [Part::Box] Box312  label="Cube307"
  Height = 35
  Length = 55
  Placement = pos=(83,11,27) rot=(0,0,1;0rad)
  Width = 146
FEATURE [Part::Cut] Cut189
  Base = -> Box311
  Placement = pos=(1,0,1) rot=(0,0,1;0rad)
  Tool = -> Box312
FEATURE [Part::Box] Box314  label="Cube309"
  Height = 45
  Length = 5
  Placement = pos=(16,56,5) rot=(0,0,1;0rad)
  Width = 56
FEATURE [Part::Fillet] Fillet181
  Base = -> Box314
  Edges = 2 edges r=3: [Edge10,Edge12]
  Placement = pos=(67,0,0) rot=(0,0,1;0rad)
FEATURE [Part::Box] Box315  label="Cube310"
  Height = 45
  Length = 5
  Placement = pos=(81,78,7) rot=(0,0,1;0rad)
  Width = 12
FEATURE [Part::Fillet] Fillet182
  Base = -> Box315
  Edges = 2 edges r=3: [Edge10,Edge12]
FEATURE [Part::MultiFuse] Fusion169
  Shapes = -> [Fillet181,Fillet182]
FEATURE [Part::Cut] Cut190
  Base = -> Cut189
  Tool = -> Fusion169
FEATURE [Part::Box] Box316  label="Cube311"
  Height = 1
  Length = 49
  Placement = pos=(86,13,64) rot=(0,0,1;0rad)
  Width = 142
FEATURE [Part::Cut] Cut191
  Base = -> Cut190
  Tool = -> Box316
FEATURE [Part::Fillet] Fillet183
  Base = -> Cut191
  Edges = 4 edges r=1.5: [Edge1,Edge15,Edge16,Edge17]
FEATURE [Part::Fillet] Fillet184
  Base = -> Fillet183
  Edges = 4 edges r=0.99: [Edge58,Edge59,Edge60,Edge61]
FEATURE [Part::Fillet] Fillet185
  Base = -> Fillet184
  Edges = 2 edges r=1: [Edge33,Edge35]
